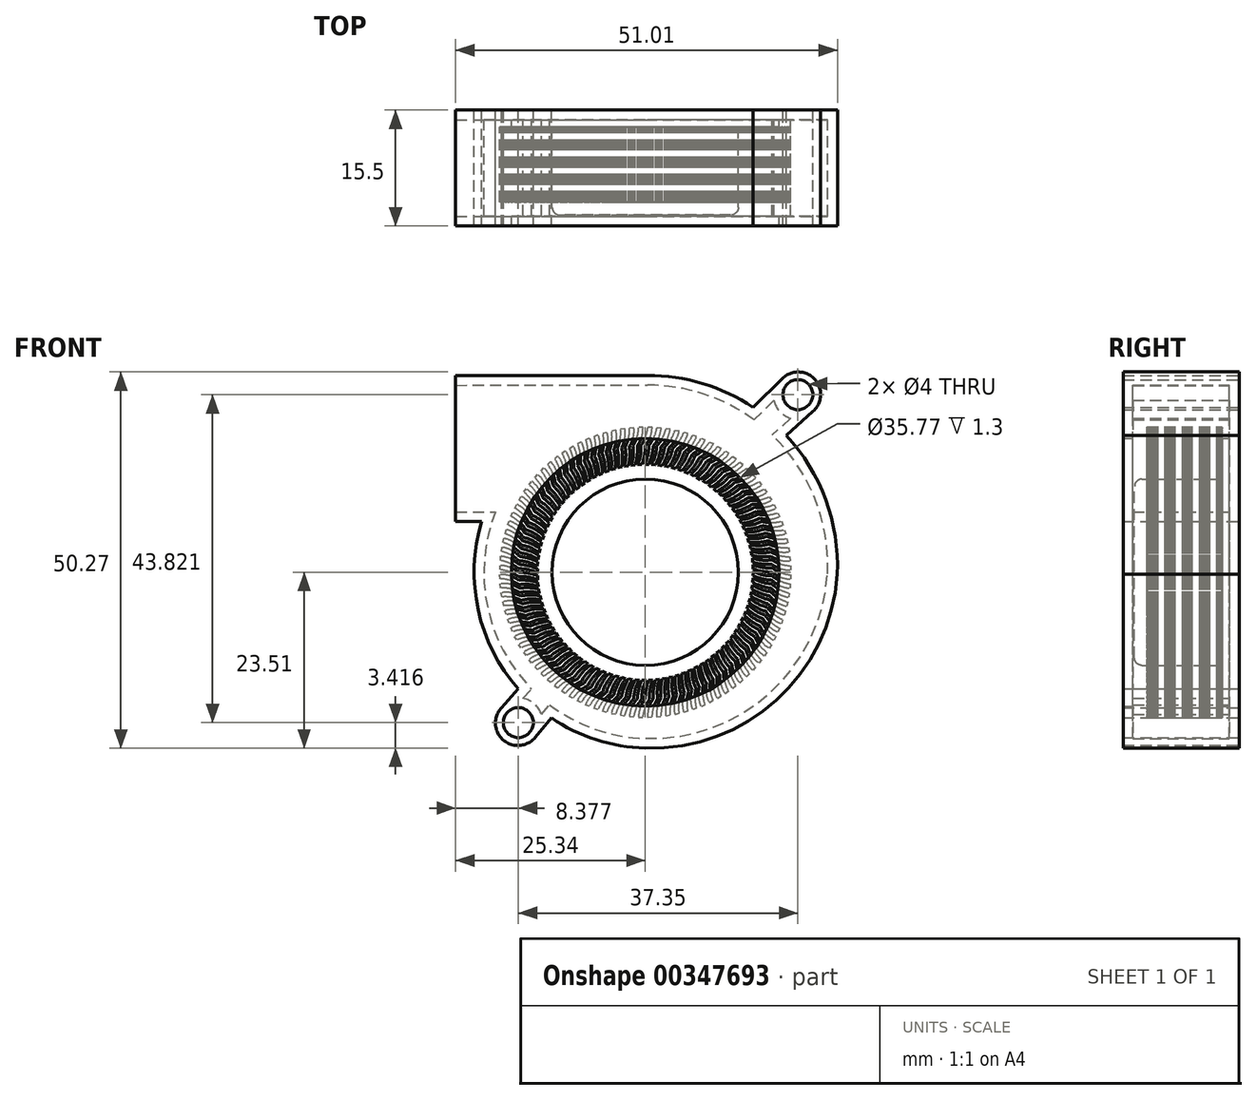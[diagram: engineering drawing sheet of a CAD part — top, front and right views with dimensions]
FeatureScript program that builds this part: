
annotation { "Feature Type Name" : "Feature", "Feature Type Description" : "" }
export const myFeature = defineFeature(function(context is Context, id is Id, definition is map)
    precondition{}
    {
        {
            var Q0;
            Q0=qCreatedBy(makeId("Front.planeOp"),FACE);
            var sketch = newSketch(context, id + "F0", { "sketchPlane" : qUnion([Q0])});
            skCircle(sketch, "E0", {"center": v(0, 0) * mm, "radius": 12.44 * mm});
            skCircle(sketch, "E1", {"center": v(0, 0) * mm, "radius": 15.98 * mm});
            skCircle(sketch, "E2.0", {"center": v(0, 0) * mm, "radius": 17.88 * mm});
            skLineSegment(sketch, "E3", {"start": v(-25.34, 6.78) * mm, "end": v(-25.34, 26.28) * mm});
            skLineSegment(sketch, "E4", {"start": v(-25.34, 6.78) * mm, "end": v(-21.86, 6.78) * mm});
            skLineSegment(sketch, "E5", {"start": v(-25.34, 26.28) * mm, "end": v(0.29, 26.3) * mm});
            skArc(sketch, "E6", {"start": v(25.64, -0.28) * mm, "mid": v(18.67, 18.45) * mm, "end": v(0.29, 26.3) * mm});
            skArc(sketch, "E7", {"start": v(0, -23.5) * mm, "mid": v(17.52, -17.08) * mm, "end": v(25.64, -0.28) * mm});
            skArc(sketch, "E8", {"start": v(-21.86, 6.78) * mm, "mid": v(-18.42, -13.77) * mm, "end": v(0, -23.5) * mm});
            skCircle(sketch, "E9", {"center": v(20.39, 23.73) * mm, "radius": 2 * mm});
            skCircle(sketch, "E10", {"center": v(-16.96, -20.1) * mm, "radius": 2 * mm});
            skLineSegment(sketch, "E11", {"start": v(22.42, 21.52) * mm, "end": v(18.83, 18.28) * mm});
            skLineSegment(sketch, "E12", {"start": v(18.32, 25.9) * mm, "end": v(14.4, 22.03) * mm});
            skArc(sketch, "E13", {"start": v(22.42, 21.52) * mm, "mid": v(22.61, 25.82) * mm, "end": v(18.32, 25.9) * mm});
            skLineSegment(sketch, "E14", {"start": v(-19.2, -18.1) * mm, "end": v(-16.96, -15.6) * mm});
            skLineSegment(sketch, "E15", {"start": v(-14.7, -22.06) * mm, "end": v(-12.56, -19.47) * mm});
            skArc(sketch, "E16", {"start": v(-19.2, -18.1) * mm, "mid": v(-19, -22.4) * mm, "end": v(-14.7, -22.06) * mm});
            skSolve(sketch);
        }
        {
            var Q0;
            Q0=makeQuery(id+"F0.imprint","IMPRINT",FACE,{"disambiguationData":[TD([[makeQuery(id+"F0.imprint","IMPRINT",EDGE,{"derivedFrom":sQuery(id+"F0.wireOp",EDGE,"E2.0")}),-1.0]])]});
            var Q1;
            Q1=makeQuery(id+"F0.imprint","IMPRINT",FACE,{"disambiguationData":[TD([[makeQuery(id+"F0.imprint","IMPRINT",EDGE,{"derivedFrom":sQuery(id+"F0.wireOp",EDGE,"E9")}),-1.0]])]});
            var Q2;
            Q2=makeQuery(id+"F0.imprint","IMPRINT",FACE,{"disambiguationData":[TD([[makeQuery(id+"F0.imprint","IMPRINT",EDGE,{"derivedFrom":sQuery(id+"F0.wireOp",EDGE,"E10")}),-1.0]])]});
            extrude(context, id + "F1", {"entities" : qUnion([Q0, Q1, Q2]), "depth" : 15.5 * mm});
        }
        {
            var Q0;
            Q0=makeQuery(id+"F1.opExtrude","SWEPT_FACE",FACE,{"disambiguationData":[OSD([sQuery(id+"F0.wireOp",EDGE,"E3")])]});
            var Q1;
            Q1=makeQuery(id+"F1.opExtrude","SWEPT_FACE",FACE,{"disambiguationData":[OSD([sQuery(id+"F0.wireOp",EDGE,"E2.0")])]});
            shell(context, id + "F2", {"entities" : qUnion([Q0, Q1]), "thickness" : 1.3 * mm});
        }
        {
            var Q0;
            Q0=makeQuery(id+"F0.imprint","IMPRINT",FACE,{"disambiguationData":[TD([[makeQuery(id+"F0.imprint","IMPRINT",EDGE,{"derivedFrom":sQuery(id+"F0.wireOp",EDGE,"E0")}),-1.0]])]});
            var Q1;
            Q1=makeQuery(id+"F0.imprint","IMPRINT",FACE,{"disambiguationData":[TD([[makeQuery(id+"F0.imprint","IMPRINT",EDGE,{"derivedFrom":sQuery(id+"F0.wireOp",EDGE,"E0")}),1.0]])]});
            extrude(context, id + "F3", {"entities" : qUnion([Q0, Q1]), "operationType" : NewBodyOperationType.ADD, "depth" : 1.3 * mm});
        }
        {
            var Q0;
            Q0=makeQuery(id+"F0.imprint","IMPRINT",FACE,{"disambiguationData":[TD([[makeQuery(id+"F0.imprint","IMPRINT",EDGE,{"derivedFrom":sQuery(id+"F0.wireOp",EDGE,"E1")}),-1.0]])]});
            var Q1;
            Q1=makeQuery(id+"F0.imprint","IMPRINT",FACE,{"disambiguationData":[TD([[makeQuery(id+"F0.imprint","IMPRINT",EDGE,{"derivedFrom":sQuery(id+"F0.wireOp",EDGE,"E0")}),-1.0]])]});
            var Q2;
            Q2=makeQuery(id+"F0.imprint","IMPRINT",FACE,{"disambiguationData":[TD([[makeQuery(id+"F0.imprint","IMPRINT",EDGE,{"derivedFrom":sQuery(id+"F0.wireOp",EDGE,"E0")}),1.0]])]});
            extrude(context, id + "F4", {"entities" : qUnion([Q0, Q1, Q2]), "depth" : 2.3 * mm});
        }
        {
            var Q0;
            Q0=makeQuery(id+"F0.imprint","IMPRINT",FACE,{"disambiguationData":[TD([[makeQuery(id+"F0.imprint","IMPRINT",EDGE,{"derivedFrom":sQuery(id+"F0.wireOp",EDGE,"E0")}),1.0]])]});
            extrude(context, id + "F5", {"entities" : qUnion([Q0]), "operationType" : NewBodyOperationType.ADD, "depth" : 14 * mm});
        }
        {
            var Q0;
            Q0=makeQuery(id+"F5.opExtrude","CAP_FACE",FACE,{"disambiguationData":[OSD([sQuery(id+"F0.wireOp",EDGE,"E0")])],"isStart":false});
            fillet(context, id + "F6", {"entities" : qUnion([Q0]), "radius" : 1 * mm, "tangentPropagation" : true, "allowEdgeOverflow" : false});
        }
        {
            var Q0;
            Q0=makeQuery(id+"F0.imprint","IMPRINT",FACE,{"disambiguationData":[TD([[makeQuery(id+"F0.imprint","IMPRINT",EDGE,{"derivedFrom":sQuery(id+"F0.wireOp",EDGE,"E1")}),-1.0]])]});
            extrude(context, id + "F7", {"entities" : qUnion([Q0]), "operationType" : NewBodyOperationType.ADD, "depth" : 1.3 * mm});
        }
        {
            var Q0;
            Q0=makeQuery(id+"F4.opExtrude","CAP_FACE",FACE,{"disambiguationData":[OSD([sQuery(id+"F0.wireOp",EDGE,"E2.0")])],"isStart":false});
            var sketch = newSketch(context, id + "F8", { "sketchPlane" : qUnion([Q0])});
            skLineSegment(sketch, "E17", {"start": v(-0.45, 14.4) * mm, "end": v(-1.01, 14.4) * mm});
            skLineSegment(sketch, "E18.MirrorCS", {"start": v(0.34, 19.42) * mm, "end": v(0.91, 19.42) * mm});
            skArc(sketch, "E19", {"start": v(-1.01, 14.4) * mm, "mid": v(-0.64, 15.64) * mm, "end": v(-0.6, 16.93) * mm});
            skArc(sketch, "E20", {"start": v(-0.6, 16.93) * mm, "mid": v(0.04, 18.11) * mm, "end": v(0.34, 19.42) * mm});
            skArc(sketch, "E21", {"start": v(0, 16.93) * mm, "mid": v(0.67, 18.1) * mm, "end": v(0.91, 19.42) * mm});
            skArc(sketch, "E22", {"start": v(-0.45, 14.4) * mm, "mid": v(-0.11, 15.65) * mm, "end": v(0, 16.93) * mm});
            skArc(sketch, "E23.1.0", {"start": v(-1.91, 14.31) * mm, "mid": v(-1.62, 15.57) * mm, "end": v(-1.66, 16.86) * mm});
            skArc(sketch, "E23.1.1", {"start": v(-1.66, 16.86) * mm, "mid": v(-1.1, 18.08) * mm, "end": v(-0.87, 19.4) * mm});
            skArc(sketch, "E23.1.2", {"start": v(-1.35, 14.35) * mm, "mid": v(-1.1, 15.61) * mm, "end": v(-1.06, 16.9) * mm});
            skArc(sketch, "E23.1.3", {"start": v(-1.06, 16.9) * mm, "mid": v(-0.47, 18.1) * mm, "end": v(-0.31, 19.44) * mm});
            skLineSegment(sketch, "E23.1.4", {"start": v(-1.35, 14.35) * mm, "end": v(-1.91, 14.31) * mm});
            skLineSegment(sketch, "E23.1.5", {"start": v(-0.87, 19.4) * mm, "end": v(-0.31, 19.44) * mm});
            skArc(sketch, "E23.2.0", {"start": v(-2.8, 14.16) * mm, "mid": v(-2.6, 15.44) * mm, "end": v(-2.71, 16.73) * mm});
            skArc(sketch, "E23.2.1", {"start": v(-2.71, 16.73) * mm, "mid": v(-2.23, 17.97) * mm, "end": v(-2.1, 19.3) * mm});
            skArc(sketch, "E23.2.2", {"start": v(-2.25, 14.23) * mm, "mid": v(-2.07, 15.51) * mm, "end": v(-2.12, 16.8) * mm});
            skArc(sketch, "E23.2.3", {"start": v(-2.12, 16.8) * mm, "mid": v(-1.6, 18.04) * mm, "end": v(-1.53, 19.38) * mm});
            skLineSegment(sketch, "E23.2.4", {"start": v(-2.25, 14.23) * mm, "end": v(-2.8, 14.16) * mm});
            skLineSegment(sketch, "E23.2.5", {"start": v(-2.1, 19.3) * mm, "end": v(-1.53, 19.38) * mm});
            skArc(sketch, "E23.3.0", {"start": v(-3.7, 13.96) * mm, "mid": v(-3.56, 15.24) * mm, "end": v(-3.76, 16.52) * mm});
            skArc(sketch, "E23.3.1", {"start": v(-3.76, 16.52) * mm, "mid": v(-3.35, 17.8) * mm, "end": v(-3.3, 19.14) * mm});
            skArc(sketch, "E23.3.2", {"start": v(-3.14, 14.06) * mm, "mid": v(-3.04, 15.35) * mm, "end": v(-3.17, 16.64) * mm});
            skArc(sketch, "E23.3.3", {"start": v(-3.17, 16.64) * mm, "mid": v(-2.74, 17.9) * mm, "end": v(-2.74, 19.24) * mm});
            skLineSegment(sketch, "E23.3.4", {"start": v(-3.14, 14.06) * mm, "end": v(-3.7, 13.96) * mm});
            skLineSegment(sketch, "E23.3.5", {"start": v(-3.3, 19.14) * mm, "end": v(-2.74, 19.24) * mm});
            skArc(sketch, "E23.4.0", {"start": v(-4.56, 13.7) * mm, "mid": v(-4.5, 15) * mm, "end": v(-4.79, 16.26) * mm});
            skArc(sketch, "E23.4.1", {"start": v(-4.79, 16.26) * mm, "mid": v(-4.46, 17.55) * mm, "end": v(-4.5, 18.9) * mm});
            skArc(sketch, "E23.4.2", {"start": v(-4.01, 13.84) * mm, "mid": v(-4, 15.13) * mm, "end": v(-4.21, 16.4) * mm});
            skArc(sketch, "E23.4.3", {"start": v(-4.21, 16.4) * mm, "mid": v(-3.85, 17.7) * mm, "end": v(-3.95, 19.03) * mm});
            skLineSegment(sketch, "E23.4.4", {"start": v(-4.01, 13.84) * mm, "end": v(-4.56, 13.7) * mm});
            skLineSegment(sketch, "E23.4.5", {"start": v(-4.5, 18.9) * mm, "end": v(-3.95, 19.03) * mm});
            skArc(sketch, "E23.5.0", {"start": v(-5.41, 13.38) * mm, "mid": v(-5.44, 14.68) * mm, "end": v(-5.8, 15.92) * mm});
            skArc(sketch, "E23.5.1", {"start": v(-5.8, 15.92) * mm, "mid": v(-5.56, 17.24) * mm, "end": v(-5.67, 18.57) * mm});
            skArc(sketch, "E23.5.2", {"start": v(-4.87, 13.56) * mm, "mid": v(-4.94, 14.85) * mm, "end": v(-5.23, 16.1) * mm});
            skArc(sketch, "E23.5.3", {"start": v(-5.23, 16.1) * mm, "mid": v(-4.96, 17.42) * mm, "end": v(-5.13, 18.75) * mm});
            skLineSegment(sketch, "E23.5.4", {"start": v(-4.87, 13.56) * mm, "end": v(-5.41, 13.38) * mm});
            skLineSegment(sketch, "E23.5.5", {"start": v(-5.67, 18.57) * mm, "end": v(-5.13, 18.75) * mm});
            skArc(sketch, "E23.6.0", {"start": v(-6.24, 13.02) * mm, "mid": v(-6.35, 14.3) * mm, "end": v(-6.79, 15.53) * mm});
            skArc(sketch, "E23.6.1", {"start": v(-6.79, 15.53) * mm, "mid": v(-6.63, 16.86) * mm, "end": v(-6.83, 18.18) * mm});
            skArc(sketch, "E23.6.2", {"start": v(-5.72, 13.23) * mm, "mid": v(-5.87, 14.5) * mm, "end": v(-6.23, 15.75) * mm});
            skArc(sketch, "E23.6.3", {"start": v(-6.23, 15.75) * mm, "mid": v(-6.04, 17.07) * mm, "end": v(-6.3, 18.39) * mm});
            skLineSegment(sketch, "E23.6.4", {"start": v(-5.72, 13.23) * mm, "end": v(-6.24, 13.02) * mm});
            skLineSegment(sketch, "E23.6.5", {"start": v(-6.83, 18.18) * mm, "end": v(-6.3, 18.39) * mm});
            skArc(sketch, "E23.7.0", {"start": v(-7.05, 12.6) * mm, "mid": v(-7.24, 13.88) * mm, "end": v(-7.75, 15.07) * mm});
            skArc(sketch, "E23.7.1", {"start": v(-7.75, 15.07) * mm, "mid": v(-7.67, 16.4) * mm, "end": v(-7.95, 17.72) * mm});
            skArc(sketch, "E23.7.2", {"start": v(-6.54, 12.84) * mm, "mid": v(-6.76, 14.11) * mm, "end": v(-7.21, 15.32) * mm});
            skArc(sketch, "E23.7.3", {"start": v(-7.21, 15.32) * mm, "mid": v(-7.1, 16.66) * mm, "end": v(-7.44, 17.96) * mm});
            skLineSegment(sketch, "E23.7.4", {"start": v(-6.54, 12.84) * mm, "end": v(-7.05, 12.6) * mm});
            skLineSegment(sketch, "E23.7.5", {"start": v(-7.95, 17.72) * mm, "end": v(-7.44, 17.96) * mm});
            skArc(sketch, "E23.8.0", {"start": v(-7.83, 12.13) * mm, "mid": v(-8.1, 13.4) * mm, "end": v(-8.68, 14.55) * mm});
            skArc(sketch, "E23.8.1", {"start": v(-8.68, 14.55) * mm, "mid": v(-8.69, 15.9) * mm, "end": v(-9.05, 17.18) * mm});
            skArc(sketch, "E23.8.2", {"start": v(-7.33, 12.4) * mm, "mid": v(-7.64, 13.66) * mm, "end": v(-8.16, 14.84) * mm});
            skArc(sketch, "E23.8.3", {"start": v(-8.16, 14.84) * mm, "mid": v(-8.13, 16.18) * mm, "end": v(-8.56, 17.45) * mm});
            skLineSegment(sketch, "E23.8.4", {"start": v(-7.33, 12.4) * mm, "end": v(-7.83, 12.13) * mm});
            skLineSegment(sketch, "E23.8.5", {"start": v(-9.05, 17.18) * mm, "end": v(-8.56, 17.45) * mm});
            skArc(sketch, "E23.9.0", {"start": v(-8.57, 11.62) * mm, "mid": v(-8.92, 12.86) * mm, "end": v(-9.58, 13.98) * mm});
            skArc(sketch, "E23.9.1", {"start": v(-9.58, 13.98) * mm, "mid": v(-9.67, 15.32) * mm, "end": v(-10.11, 16.58) * mm});
            skArc(sketch, "E23.9.2", {"start": v(-8.1, 11.92) * mm, "mid": v(-8.48, 13.15) * mm, "end": v(-9.07, 14.3) * mm});
            skArc(sketch, "E23.9.3", {"start": v(-9.07, 14.3) * mm, "mid": v(-9.13, 15.64) * mm, "end": v(-9.63, 16.88) * mm});
            skLineSegment(sketch, "E23.9.4", {"start": v(-8.1, 11.92) * mm, "end": v(-8.57, 11.62) * mm});
            skLineSegment(sketch, "E23.9.5", {"start": v(-10.11, 16.58) * mm, "end": v(-9.63, 16.88) * mm});
            skArc(sketch, "E23.10.0", {"start": v(-9.28, 11.06) * mm, "mid": v(-9.7, 12.28) * mm, "end": v(-10.43, 13.35) * mm});
            skArc(sketch, "E23.10.1", {"start": v(-10.43, 13.35) * mm, "mid": v(-10.61, 14.68) * mm, "end": v(-11.13, 15.91) * mm});
            skArc(sketch, "E23.10.2", {"start": v(-8.83, 11.39) * mm, "mid": v(-9.29, 12.6) * mm, "end": v(-9.95, 13.7) * mm});
            skArc(sketch, "E23.10.3", {"start": v(-9.95, 13.7) * mm, "mid": v(-10.1, 15.03) * mm, "end": v(-10.68, 16.24) * mm});
            skLineSegment(sketch, "E23.10.4", {"start": v(-8.83, 11.39) * mm, "end": v(-9.28, 11.06) * mm});
            skLineSegment(sketch, "E23.10.5", {"start": v(-11.13, 15.91) * mm, "end": v(-10.68, 16.24) * mm});
            skArc(sketch, "E23.11.0", {"start": v(-9.96, 10.45) * mm, "mid": v(-10.46, 11.65) * mm, "end": v(-11.25, 12.67) * mm});
            skArc(sketch, "E23.11.1", {"start": v(-11.25, 12.67) * mm, "mid": v(-11.51, 13.98) * mm, "end": v(-12.11, 15.18) * mm});
            skArc(sketch, "E23.11.2", {"start": v(-9.52, 10.81) * mm, "mid": v(-10.06, 11.99) * mm, "end": v(-10.8, 13.05) * mm});
            skArc(sketch, "E23.11.3", {"start": v(-10.8, 13.05) * mm, "mid": v(-11.02, 14.37) * mm, "end": v(-11.67, 15.54) * mm});
            skLineSegment(sketch, "E23.11.4", {"start": v(-9.52, 10.81) * mm, "end": v(-9.96, 10.45) * mm});
            skLineSegment(sketch, "E23.11.5", {"start": v(-12.11, 15.18) * mm, "end": v(-11.67, 15.54) * mm});
            skArc(sketch, "E23.12.0", {"start": v(-10.6, 9.8) * mm, "mid": v(-11.17, 10.97) * mm, "end": v(-12.03, 11.94) * mm});
            skArc(sketch, "E23.12.1", {"start": v(-12.03, 11.94) * mm, "mid": v(-12.37, 13.23) * mm, "end": v(-13.04, 14.39) * mm});
            skArc(sketch, "E23.12.2", {"start": v(-10.18, 10.2) * mm, "mid": v(-10.8, 11.33) * mm, "end": v(-11.6, 12.35) * mm});
            skArc(sketch, "E23.12.3", {"start": v(-11.6, 12.35) * mm, "mid": v(-11.9, 13.65) * mm, "end": v(-12.63, 14.78) * mm});
            skLineSegment(sketch, "E23.12.4", {"start": v(-10.18, 10.2) * mm, "end": v(-10.6, 9.8) * mm});
            skLineSegment(sketch, "E23.12.5", {"start": v(-13.04, 14.39) * mm, "end": v(-12.63, 14.78) * mm});
            skArc(sketch, "E23.13.0", {"start": v(-11.2, 9.12) * mm, "mid": v(-11.84, 10.24) * mm, "end": v(-12.75, 11.16) * mm});
            skArc(sketch, "E23.13.1", {"start": v(-12.75, 11.16) * mm, "mid": v(-13.17, 12.43) * mm, "end": v(-13.92, 13.54) * mm});
            skArc(sketch, "E23.13.2", {"start": v(-10.8, 9.53) * mm, "mid": v(-11.48, 10.63) * mm, "end": v(-12.35, 11.6) * mm});
            skArc(sketch, "E23.13.3", {"start": v(-12.35, 11.6) * mm, "mid": v(-12.74, 12.88) * mm, "end": v(-13.53, 13.96) * mm});
            skLineSegment(sketch, "E23.13.4", {"start": v(-10.8, 9.53) * mm, "end": v(-11.2, 9.12) * mm});
            skLineSegment(sketch, "E23.13.5", {"start": v(-13.92, 13.54) * mm, "end": v(-13.53, 13.96) * mm});
            skArc(sketch, "E23.14.0", {"start": v(-11.74, 8.4) * mm, "mid": v(-12.46, 9.48) * mm, "end": v(-13.43, 10.34) * mm});
            skArc(sketch, "E23.14.1", {"start": v(-13.43, 10.34) * mm, "mid": v(-13.93, 11.58) * mm, "end": v(-14.74, 12.64) * mm});
            skArc(sketch, "E23.14.2", {"start": v(-11.38, 8.84) * mm, "mid": v(-12.13, 9.89) * mm, "end": v(-13.05, 10.8) * mm});
            skArc(sketch, "E23.14.3", {"start": v(-13.05, 10.8) * mm, "mid": v(-13.52, 12.05) * mm, "end": v(-14.38, 13.08) * mm});
            skLineSegment(sketch, "E23.14.4", {"start": v(-11.38, 8.84) * mm, "end": v(-11.74, 8.4) * mm});
            skLineSegment(sketch, "E23.14.5", {"start": v(-14.74, 12.64) * mm, "end": v(-14.38, 13.08) * mm});
            skArc(sketch, "E23.15.0", {"start": v(-12.25, 7.65) * mm, "mid": v(-13.03, 8.68) * mm, "end": v(-14.05, 9.47) * mm});
            skArc(sketch, "E23.15.1", {"start": v(-14.05, 9.47) * mm, "mid": v(-14.63, 10.68) * mm, "end": v(-15.5, 11.7) * mm});
            skArc(sketch, "E23.15.2", {"start": v(-11.91, 8.1) * mm, "mid": v(-12.73, 9.1) * mm, "end": v(-13.7, 9.95) * mm});
            skArc(sketch, "E23.15.3", {"start": v(-13.7, 9.95) * mm, "mid": v(-14.25, 11.18) * mm, "end": v(-15.17, 12.15) * mm});
            skLineSegment(sketch, "E23.15.4", {"start": v(-11.91, 8.1) * mm, "end": v(-12.25, 7.65) * mm});
            skLineSegment(sketch, "E23.15.5", {"start": v(-15.5, 11.7) * mm, "end": v(-15.17, 12.15) * mm});
            skArc(sketch, "E23.16.0", {"start": v(-12.7, 6.86) * mm, "mid": v(-13.55, 7.84) * mm, "end": v(-14.62, 8.57) * mm});
            skArc(sketch, "E23.16.1", {"start": v(-14.62, 8.57) * mm, "mid": v(-15.27, 9.74) * mm, "end": v(-16.2, 10.7) * mm});
            skArc(sketch, "E23.16.2", {"start": v(-12.4, 7.34) * mm, "mid": v(-13.27, 8.3) * mm, "end": v(-14.3, 9.07) * mm});
            skArc(sketch, "E23.16.3", {"start": v(-14.3, 9.07) * mm, "mid": v(-14.92, 10.26) * mm, "end": v(-15.9, 11.17) * mm});
            skLineSegment(sketch, "E23.16.4", {"start": v(-12.4, 7.34) * mm, "end": v(-12.7, 6.86) * mm});
            skLineSegment(sketch, "E23.16.5", {"start": v(-16.2, 10.7) * mm, "end": v(-15.9, 11.17) * mm});
            skArc(sketch, "E23.17.0", {"start": v(-13.1, 6.05) * mm, "mid": v(-14.01, 6.98) * mm, "end": v(-15.13, 7.64) * mm});
            skArc(sketch, "E23.17.1", {"start": v(-15.13, 7.64) * mm, "mid": v(-15.85, 8.76) * mm, "end": v(-16.85, 9.66) * mm});
            skArc(sketch, "E23.17.2", {"start": v(-12.84, 6.55) * mm, "mid": v(-13.77, 7.44) * mm, "end": v(-14.84, 8.16) * mm});
            skArc(sketch, "E23.17.3", {"start": v(-14.84, 8.16) * mm, "mid": v(-15.54, 9.3) * mm, "end": v(-16.58, 10.15) * mm});
            skLineSegment(sketch, "E23.17.4", {"start": v(-12.84, 6.55) * mm, "end": v(-13.1, 6.05) * mm});
            skLineSegment(sketch, "E23.17.5", {"start": v(-16.85, 9.66) * mm, "end": v(-16.58, 10.15) * mm});
            skArc(sketch, "E23.18.0", {"start": v(-13.46, 5.22) * mm, "mid": v(-14.42, 6.08) * mm, "end": v(-15.58, 6.67) * mm});
            skArc(sketch, "E23.18.1", {"start": v(-15.58, 6.67) * mm, "mid": v(-16.37, 7.75) * mm, "end": v(-17.42, 8.58) * mm});
            skArc(sketch, "E23.18.2", {"start": v(-13.22, 5.73) * mm, "mid": v(-14.2, 6.56) * mm, "end": v(-15.32, 7.21) * mm});
            skArc(sketch, "E23.18.3", {"start": v(-15.32, 7.21) * mm, "mid": v(-16.1, 8.3) * mm, "end": v(-17.18, 9.1) * mm});
            skLineSegment(sketch, "E23.18.4", {"start": v(-13.22, 5.73) * mm, "end": v(-13.46, 5.22) * mm});
            skLineSegment(sketch, "E23.18.5", {"start": v(-17.42, 8.58) * mm, "end": v(-17.18, 9.1) * mm});
            skArc(sketch, "E23.19.0", {"start": v(-13.76, 4.36) * mm, "mid": v(-14.78, 5.16) * mm, "end": v(-15.96, 5.68) * mm});
            skArc(sketch, "E23.19.1", {"start": v(-15.96, 5.68) * mm, "mid": v(-16.82, 6.7) * mm, "end": v(-17.93, 7.47) * mm});
            skArc(sketch, "E23.19.2", {"start": v(-13.55, 4.89) * mm, "mid": v(-14.6, 5.66) * mm, "end": v(-15.75, 6.23) * mm});
            skArc(sketch, "E23.19.3", {"start": v(-15.75, 6.23) * mm, "mid": v(-16.58, 7.28) * mm, "end": v(-17.72, 8) * mm});
            skLineSegment(sketch, "E23.19.4", {"start": v(-13.55, 4.89) * mm, "end": v(-13.76, 4.36) * mm});
            skLineSegment(sketch, "E23.19.5", {"start": v(-17.93, 7.47) * mm, "end": v(-17.72, 8) * mm});
            skArc(sketch, "E23.20.0", {"start": v(-14, 3.49) * mm, "mid": v(-15.07, 4.23) * mm, "end": v(-16.29, 4.67) * mm});
            skArc(sketch, "E23.20.1", {"start": v(-16.29, 4.67) * mm, "mid": v(-17.21, 5.64) * mm, "end": v(-18.36, 6.33) * mm});
            skArc(sketch, "E23.20.2", {"start": v(-13.84, 4.03) * mm, "mid": v(-14.92, 4.73) * mm, "end": v(-16.1, 5.23) * mm});
            skArc(sketch, "E23.20.3", {"start": v(-16.1, 5.23) * mm, "mid": v(-17, 6.23) * mm, "end": v(-18.18, 6.87) * mm});
            skLineSegment(sketch, "E23.20.4", {"start": v(-13.84, 4.03) * mm, "end": v(-14, 3.49) * mm});
            skLineSegment(sketch, "E23.20.5", {"start": v(-18.36, 6.33) * mm, "end": v(-18.18, 6.87) * mm});
            skArc(sketch, "E23.21.0", {"start": v(-14.2, 2.6) * mm, "mid": v(-15.3, 3.27) * mm, "end": v(-16.55, 3.64) * mm});
            skArc(sketch, "E23.21.1", {"start": v(-16.55, 3.64) * mm, "mid": v(-17.53, 4.55) * mm, "end": v(-18.72, 5.16) * mm});
            skArc(sketch, "E23.21.2", {"start": v(-14.06, 3.15) * mm, "mid": v(-15.19, 3.78) * mm, "end": v(-16.4, 4.21) * mm});
            skArc(sketch, "E23.21.3", {"start": v(-16.4, 4.21) * mm, "mid": v(-17.36, 5.15) * mm, "end": v(-18.58, 5.71) * mm});
            skLineSegment(sketch, "E23.21.4", {"start": v(-14.06, 3.15) * mm, "end": v(-14.2, 2.6) * mm});
            skLineSegment(sketch, "E23.21.5", {"start": v(-18.72, 5.16) * mm, "end": v(-18.58, 5.71) * mm});
            skArc(sketch, "E23.22.0", {"start": v(-14.34, 1.7) * mm, "mid": v(-15.48, 2.3) * mm, "end": v(-16.75, 2.59) * mm});
            skArc(sketch, "E23.22.1", {"start": v(-16.75, 2.59) * mm, "mid": v(-17.78, 3.44) * mm, "end": v(-19, 3.98) * mm});
            skArc(sketch, "E23.22.2", {"start": v(-14.23, 2.26) * mm, "mid": v(-15.4, 2.82) * mm, "end": v(-16.64, 3.17) * mm});
            skArc(sketch, "E23.22.3", {"start": v(-16.64, 3.17) * mm, "mid": v(-17.65, 4.05) * mm, "end": v(-18.9, 4.53) * mm});
            skLineSegment(sketch, "E23.22.4", {"start": v(-14.23, 2.26) * mm, "end": v(-14.34, 1.7) * mm});
            skLineSegment(sketch, "E23.22.5", {"start": v(-19, 3.98) * mm, "end": v(-18.9, 4.53) * mm});
            skArc(sketch, "E23.23.0", {"start": v(-14.42, 0.8) * mm, "mid": v(-15.6, 1.33) * mm, "end": v(-16.88, 1.53) * mm});
            skArc(sketch, "E23.23.1", {"start": v(-16.88, 1.53) * mm, "mid": v(-17.96, 2.31) * mm, "end": v(-19.22, 2.78) * mm});
            skArc(sketch, "E23.23.2", {"start": v(-14.34, 1.36) * mm, "mid": v(-15.54, 1.85) * mm, "end": v(-16.8, 2.12) * mm});
            skArc(sketch, "E23.23.3", {"start": v(-16.8, 2.12) * mm, "mid": v(-17.87, 2.93) * mm, "end": v(-19.15, 3.34) * mm});
            skLineSegment(sketch, "E23.23.4", {"start": v(-14.34, 1.36) * mm, "end": v(-14.42, 0.8) * mm});
            skLineSegment(sketch, "E23.23.5", {"start": v(-19.22, 2.78) * mm, "end": v(-19.15, 3.34) * mm});
            skArc(sketch, "E23.24.0", {"start": v(-14.44, -0.1) * mm, "mid": v(-15.65, 0.35) * mm, "end": v(-16.94, 0.47) * mm});
            skArc(sketch, "E23.24.1", {"start": v(-16.94, 0.47) * mm, "mid": v(-18.07, 1.18) * mm, "end": v(-19.36, 1.56) * mm});
            skArc(sketch, "E23.24.2", {"start": v(-14.4, 0.46) * mm, "mid": v(-15.63, 0.87) * mm, "end": v(-16.9, 1.06) * mm});
            skArc(sketch, "E23.24.3", {"start": v(-16.9, 1.06) * mm, "mid": v(-18.02, 1.8) * mm, "end": v(-19.32, 2.13) * mm});
            skLineSegment(sketch, "E23.24.4", {"start": v(-14.4, 0.46) * mm, "end": v(-14.44, -0.1) * mm});
            skLineSegment(sketch, "E23.24.5", {"start": v(-19.36, 1.56) * mm, "end": v(-19.32, 2.13) * mm});
            skArc(sketch, "E23.25.0", {"start": v(-14.4, -1.01) * mm, "mid": v(-15.64, -0.64) * mm, "end": v(-16.93, -0.6) * mm});
            skArc(sketch, "E23.25.1", {"start": v(-16.93, -0.6) * mm, "mid": v(-18.11, 0.04) * mm, "end": v(-19.42, 0.34) * mm});
            skArc(sketch, "E23.25.2", {"start": v(-14.4, -0.45) * mm, "mid": v(-15.65, -0.11) * mm, "end": v(-16.93, 0) * mm});
            skArc(sketch, "E23.25.3", {"start": v(-16.93, 0) * mm, "mid": v(-18.1, 0.67) * mm, "end": v(-19.42, 0.91) * mm});
            skLineSegment(sketch, "E23.25.4", {"start": v(-14.4, -0.45) * mm, "end": v(-14.4, -1.01) * mm});
            skLineSegment(sketch, "E23.25.5", {"start": v(-19.42, 0.34) * mm, "end": v(-19.42, 0.91) * mm});
            skArc(sketch, "E23.26.0", {"start": v(-14.31, -1.91) * mm, "mid": v(-15.57, -1.62) * mm, "end": v(-16.86, -1.66) * mm});
            skArc(sketch, "E23.26.1", {"start": v(-16.86, -1.66) * mm, "mid": v(-18.08, -1.1) * mm, "end": v(-19.4, -0.87) * mm});
            skArc(sketch, "E23.26.2", {"start": v(-14.35, -1.35) * mm, "mid": v(-15.61, -1.1) * mm, "end": v(-16.9, -1.06) * mm});
            skArc(sketch, "E23.26.3", {"start": v(-16.9, -1.06) * mm, "mid": v(-18.1, -0.47) * mm, "end": v(-19.44, -0.31) * mm});
            skLineSegment(sketch, "E23.26.4", {"start": v(-14.35, -1.35) * mm, "end": v(-14.31, -1.91) * mm});
            skLineSegment(sketch, "E23.26.5", {"start": v(-19.4, -0.87) * mm, "end": v(-19.44, -0.31) * mm});
            skArc(sketch, "E23.27.0", {"start": v(-14.16, -2.8) * mm, "mid": v(-15.44, -2.6) * mm, "end": v(-16.73, -2.71) * mm});
            skArc(sketch, "E23.27.1", {"start": v(-16.73, -2.71) * mm, "mid": v(-17.97, -2.23) * mm, "end": v(-19.3, -2.1) * mm});
            skArc(sketch, "E23.27.2", {"start": v(-14.23, -2.25) * mm, "mid": v(-15.51, -2.07) * mm, "end": v(-16.8, -2.12) * mm});
            skArc(sketch, "E23.27.3", {"start": v(-16.8, -2.12) * mm, "mid": v(-18.04, -1.6) * mm, "end": v(-19.38, -1.53) * mm});
            skLineSegment(sketch, "E23.27.4", {"start": v(-14.23, -2.25) * mm, "end": v(-14.16, -2.8) * mm});
            skLineSegment(sketch, "E23.27.5", {"start": v(-19.3, -2.1) * mm, "end": v(-19.38, -1.53) * mm});
            skArc(sketch, "E23.28.0", {"start": v(-13.96, -3.7) * mm, "mid": v(-15.24, -3.56) * mm, "end": v(-16.52, -3.76) * mm});
            skArc(sketch, "E23.28.1", {"start": v(-16.52, -3.76) * mm, "mid": v(-17.8, -3.35) * mm, "end": v(-19.14, -3.3) * mm});
            skArc(sketch, "E23.28.2", {"start": v(-14.06, -3.14) * mm, "mid": v(-15.35, -3.04) * mm, "end": v(-16.64, -3.17) * mm});
            skArc(sketch, "E23.28.3", {"start": v(-16.64, -3.17) * mm, "mid": v(-17.9, -2.74) * mm, "end": v(-19.24, -2.74) * mm});
            skLineSegment(sketch, "E23.28.4", {"start": v(-14.06, -3.14) * mm, "end": v(-13.96, -3.7) * mm});
            skLineSegment(sketch, "E23.28.5", {"start": v(-19.14, -3.3) * mm, "end": v(-19.24, -2.74) * mm});
            skArc(sketch, "E23.29.0", {"start": v(-13.7, -4.56) * mm, "mid": v(-15, -4.5) * mm, "end": v(-16.26, -4.79) * mm});
            skArc(sketch, "E23.29.1", {"start": v(-16.26, -4.79) * mm, "mid": v(-17.55, -4.46) * mm, "end": v(-18.9, -4.5) * mm});
            skArc(sketch, "E23.29.2", {"start": v(-13.84, -4.01) * mm, "mid": v(-15.13, -4) * mm, "end": v(-16.4, -4.21) * mm});
            skArc(sketch, "E23.29.3", {"start": v(-16.4, -4.21) * mm, "mid": v(-17.7, -3.85) * mm, "end": v(-19.03, -3.95) * mm});
            skLineSegment(sketch, "E23.29.4", {"start": v(-13.84, -4.01) * mm, "end": v(-13.7, -4.56) * mm});
            skLineSegment(sketch, "E23.29.5", {"start": v(-18.9, -4.5) * mm, "end": v(-19.03, -3.95) * mm});
            skArc(sketch, "E23.30.0", {"start": v(-13.38, -5.41) * mm, "mid": v(-14.68, -5.44) * mm, "end": v(-15.92, -5.8) * mm});
            skArc(sketch, "E23.30.1", {"start": v(-15.92, -5.8) * mm, "mid": v(-17.24, -5.56) * mm, "end": v(-18.57, -5.67) * mm});
            skArc(sketch, "E23.30.2", {"start": v(-13.56, -4.87) * mm, "mid": v(-14.85, -4.94) * mm, "end": v(-16.1, -5.23) * mm});
            skArc(sketch, "E23.30.3", {"start": v(-16.1, -5.23) * mm, "mid": v(-17.42, -4.96) * mm, "end": v(-18.75, -5.13) * mm});
            skLineSegment(sketch, "E23.30.4", {"start": v(-13.56, -4.87) * mm, "end": v(-13.38, -5.41) * mm});
            skLineSegment(sketch, "E23.30.5", {"start": v(-18.57, -5.67) * mm, "end": v(-18.75, -5.13) * mm});
            skArc(sketch, "E23.31.0", {"start": v(-13.02, -6.24) * mm, "mid": v(-14.3, -6.35) * mm, "end": v(-15.53, -6.79) * mm});
            skArc(sketch, "E23.31.1", {"start": v(-15.53, -6.79) * mm, "mid": v(-16.86, -6.63) * mm, "end": v(-18.18, -6.83) * mm});
            skArc(sketch, "E23.31.2", {"start": v(-13.23, -5.72) * mm, "mid": v(-14.5, -5.87) * mm, "end": v(-15.75, -6.23) * mm});
            skArc(sketch, "E23.31.3", {"start": v(-15.75, -6.23) * mm, "mid": v(-17.07, -6.04) * mm, "end": v(-18.39, -6.3) * mm});
            skLineSegment(sketch, "E23.31.4", {"start": v(-13.23, -5.72) * mm, "end": v(-13.02, -6.24) * mm});
            skLineSegment(sketch, "E23.31.5", {"start": v(-18.18, -6.83) * mm, "end": v(-18.39, -6.3) * mm});
            skArc(sketch, "E23.32.0", {"start": v(-12.6, -7.05) * mm, "mid": v(-13.88, -7.24) * mm, "end": v(-15.07, -7.75) * mm});
            skArc(sketch, "E23.32.1", {"start": v(-15.07, -7.75) * mm, "mid": v(-16.4, -7.67) * mm, "end": v(-17.72, -7.95) * mm});
            skArc(sketch, "E23.32.2", {"start": v(-12.84, -6.54) * mm, "mid": v(-14.11, -6.76) * mm, "end": v(-15.32, -7.21) * mm});
            skArc(sketch, "E23.32.3", {"start": v(-15.32, -7.21) * mm, "mid": v(-16.66, -7.1) * mm, "end": v(-17.96, -7.44) * mm});
            skLineSegment(sketch, "E23.32.4", {"start": v(-12.84, -6.54) * mm, "end": v(-12.6, -7.05) * mm});
            skLineSegment(sketch, "E23.32.5", {"start": v(-17.72, -7.95) * mm, "end": v(-17.96, -7.44) * mm});
            skArc(sketch, "E23.33.0", {"start": v(-12.13, -7.83) * mm, "mid": v(-13.4, -8.1) * mm, "end": v(-14.55, -8.68) * mm});
            skArc(sketch, "E23.33.1", {"start": v(-14.55, -8.68) * mm, "mid": v(-15.9, -8.69) * mm, "end": v(-17.18, -9.05) * mm});
            skArc(sketch, "E23.33.2", {"start": v(-12.4, -7.33) * mm, "mid": v(-13.66, -7.64) * mm, "end": v(-14.84, -8.16) * mm});
            skArc(sketch, "E23.33.3", {"start": v(-14.84, -8.16) * mm, "mid": v(-16.18, -8.13) * mm, "end": v(-17.45, -8.56) * mm});
            skLineSegment(sketch, "E23.33.4", {"start": v(-12.4, -7.33) * mm, "end": v(-12.13, -7.83) * mm});
            skLineSegment(sketch, "E23.33.5", {"start": v(-17.18, -9.05) * mm, "end": v(-17.45, -8.56) * mm});
            skArc(sketch, "E23.34.0", {"start": v(-11.62, -8.57) * mm, "mid": v(-12.86, -8.92) * mm, "end": v(-13.98, -9.58) * mm});
            skArc(sketch, "E23.34.1", {"start": v(-13.98, -9.58) * mm, "mid": v(-15.32, -9.67) * mm, "end": v(-16.58, -10.11) * mm});
            skArc(sketch, "E23.34.2", {"start": v(-11.92, -8.1) * mm, "mid": v(-13.15, -8.48) * mm, "end": v(-14.3, -9.07) * mm});
            skArc(sketch, "E23.34.3", {"start": v(-14.3, -9.07) * mm, "mid": v(-15.64, -9.13) * mm, "end": v(-16.88, -9.63) * mm});
            skLineSegment(sketch, "E23.34.4", {"start": v(-11.92, -8.1) * mm, "end": v(-11.62, -8.57) * mm});
            skLineSegment(sketch, "E23.34.5", {"start": v(-16.58, -10.11) * mm, "end": v(-16.88, -9.63) * mm});
            skArc(sketch, "E23.35.0", {"start": v(-11.06, -9.28) * mm, "mid": v(-12.28, -9.7) * mm, "end": v(-13.35, -10.43) * mm});
            skArc(sketch, "E23.35.1", {"start": v(-13.35, -10.43) * mm, "mid": v(-14.68, -10.61) * mm, "end": v(-15.91, -11.13) * mm});
            skArc(sketch, "E23.35.2", {"start": v(-11.39, -8.83) * mm, "mid": v(-12.6, -9.29) * mm, "end": v(-13.7, -9.95) * mm});
            skArc(sketch, "E23.35.3", {"start": v(-13.7, -9.95) * mm, "mid": v(-15.03, -10.1) * mm, "end": v(-16.24, -10.68) * mm});
            skLineSegment(sketch, "E23.35.4", {"start": v(-11.39, -8.83) * mm, "end": v(-11.06, -9.28) * mm});
            skLineSegment(sketch, "E23.35.5", {"start": v(-15.91, -11.13) * mm, "end": v(-16.24, -10.68) * mm});
            skArc(sketch, "E23.36.0", {"start": v(-10.45, -9.96) * mm, "mid": v(-11.65, -10.46) * mm, "end": v(-12.67, -11.25) * mm});
            skArc(sketch, "E23.36.1", {"start": v(-12.67, -11.25) * mm, "mid": v(-13.98, -11.51) * mm, "end": v(-15.18, -12.11) * mm});
            skArc(sketch, "E23.36.2", {"start": v(-10.81, -9.52) * mm, "mid": v(-11.99, -10.06) * mm, "end": v(-13.05, -10.8) * mm});
            skArc(sketch, "E23.36.3", {"start": v(-13.05, -10.8) * mm, "mid": v(-14.37, -11.02) * mm, "end": v(-15.54, -11.67) * mm});
            skLineSegment(sketch, "E23.36.4", {"start": v(-10.81, -9.52) * mm, "end": v(-10.45, -9.96) * mm});
            skLineSegment(sketch, "E23.36.5", {"start": v(-15.18, -12.11) * mm, "end": v(-15.54, -11.67) * mm});
            skArc(sketch, "E23.37.0", {"start": v(-9.8, -10.6) * mm, "mid": v(-10.97, -11.17) * mm, "end": v(-11.94, -12.03) * mm});
            skArc(sketch, "E23.37.1", {"start": v(-11.94, -12.03) * mm, "mid": v(-13.23, -12.37) * mm, "end": v(-14.39, -13.04) * mm});
            skArc(sketch, "E23.37.2", {"start": v(-10.2, -10.18) * mm, "mid": v(-11.33, -10.8) * mm, "end": v(-12.35, -11.6) * mm});
            skArc(sketch, "E23.37.3", {"start": v(-12.35, -11.6) * mm, "mid": v(-13.65, -11.9) * mm, "end": v(-14.78, -12.63) * mm});
            skLineSegment(sketch, "E23.37.4", {"start": v(-10.2, -10.18) * mm, "end": v(-9.8, -10.6) * mm});
            skLineSegment(sketch, "E23.37.5", {"start": v(-14.39, -13.04) * mm, "end": v(-14.78, -12.63) * mm});
            skArc(sketch, "E23.38.0", {"start": v(-9.12, -11.2) * mm, "mid": v(-10.24, -11.84) * mm, "end": v(-11.16, -12.75) * mm});
            skArc(sketch, "E23.38.1", {"start": v(-11.16, -12.75) * mm, "mid": v(-12.43, -13.17) * mm, "end": v(-13.54, -13.92) * mm});
            skArc(sketch, "E23.38.2", {"start": v(-9.53, -10.8) * mm, "mid": v(-10.63, -11.48) * mm, "end": v(-11.6, -12.35) * mm});
            skArc(sketch, "E23.38.3", {"start": v(-11.6, -12.35) * mm, "mid": v(-12.88, -12.74) * mm, "end": v(-13.96, -13.53) * mm});
            skLineSegment(sketch, "E23.38.4", {"start": v(-9.53, -10.8) * mm, "end": v(-9.12, -11.2) * mm});
            skLineSegment(sketch, "E23.38.5", {"start": v(-13.54, -13.92) * mm, "end": v(-13.96, -13.53) * mm});
            skArc(sketch, "E23.39.0", {"start": v(-8.4, -11.74) * mm, "mid": v(-9.48, -12.46) * mm, "end": v(-10.34, -13.43) * mm});
            skArc(sketch, "E23.39.1", {"start": v(-10.34, -13.43) * mm, "mid": v(-11.58, -13.93) * mm, "end": v(-12.64, -14.74) * mm});
            skArc(sketch, "E23.39.2", {"start": v(-8.84, -11.38) * mm, "mid": v(-9.89, -12.13) * mm, "end": v(-10.8, -13.05) * mm});
            skArc(sketch, "E23.39.3", {"start": v(-10.8, -13.05) * mm, "mid": v(-12.05, -13.52) * mm, "end": v(-13.08, -14.38) * mm});
            skLineSegment(sketch, "E23.39.4", {"start": v(-8.84, -11.38) * mm, "end": v(-8.4, -11.74) * mm});
            skLineSegment(sketch, "E23.39.5", {"start": v(-12.64, -14.74) * mm, "end": v(-13.08, -14.38) * mm});
            skArc(sketch, "E23.40.0", {"start": v(-7.65, -12.25) * mm, "mid": v(-8.68, -13.03) * mm, "end": v(-9.47, -14.05) * mm});
            skArc(sketch, "E23.40.1", {"start": v(-9.47, -14.05) * mm, "mid": v(-10.68, -14.63) * mm, "end": v(-11.7, -15.5) * mm});
            skArc(sketch, "E23.40.2", {"start": v(-8.1, -11.91) * mm, "mid": v(-9.1, -12.73) * mm, "end": v(-9.95, -13.7) * mm});
            skArc(sketch, "E23.40.3", {"start": v(-9.95, -13.7) * mm, "mid": v(-11.18, -14.25) * mm, "end": v(-12.15, -15.17) * mm});
            skLineSegment(sketch, "E23.40.4", {"start": v(-8.1, -11.91) * mm, "end": v(-7.65, -12.25) * mm});
            skLineSegment(sketch, "E23.40.5", {"start": v(-11.7, -15.5) * mm, "end": v(-12.15, -15.17) * mm});
            skArc(sketch, "E23.41.0", {"start": v(-6.86, -12.7) * mm, "mid": v(-7.84, -13.55) * mm, "end": v(-8.57, -14.62) * mm});
            skArc(sketch, "E23.41.1", {"start": v(-8.57, -14.62) * mm, "mid": v(-9.74, -15.27) * mm, "end": v(-10.7, -16.2) * mm});
            skArc(sketch, "E23.41.2", {"start": v(-7.34, -12.4) * mm, "mid": v(-8.3, -13.27) * mm, "end": v(-9.07, -14.3) * mm});
            skArc(sketch, "E23.41.3", {"start": v(-9.07, -14.3) * mm, "mid": v(-10.26, -14.92) * mm, "end": v(-11.17, -15.9) * mm});
            skLineSegment(sketch, "E23.41.4", {"start": v(-7.34, -12.4) * mm, "end": v(-6.86, -12.7) * mm});
            skLineSegment(sketch, "E23.41.5", {"start": v(-10.7, -16.2) * mm, "end": v(-11.17, -15.9) * mm});
            skArc(sketch, "E23.42.0", {"start": v(-6.05, -13.1) * mm, "mid": v(-6.98, -14.01) * mm, "end": v(-7.64, -15.13) * mm});
            skArc(sketch, "E23.42.1", {"start": v(-7.64, -15.13) * mm, "mid": v(-8.76, -15.85) * mm, "end": v(-9.66, -16.85) * mm});
            skArc(sketch, "E23.42.2", {"start": v(-6.55, -12.84) * mm, "mid": v(-7.44, -13.77) * mm, "end": v(-8.16, -14.84) * mm});
            skArc(sketch, "E23.42.3", {"start": v(-8.16, -14.84) * mm, "mid": v(-9.3, -15.54) * mm, "end": v(-10.15, -16.58) * mm});
            skLineSegment(sketch, "E23.42.4", {"start": v(-6.55, -12.84) * mm, "end": v(-6.05, -13.1) * mm});
            skLineSegment(sketch, "E23.42.5", {"start": v(-9.66, -16.85) * mm, "end": v(-10.15, -16.58) * mm});
            skArc(sketch, "E23.43.0", {"start": v(-5.22, -13.46) * mm, "mid": v(-6.08, -14.42) * mm, "end": v(-6.67, -15.58) * mm});
            skArc(sketch, "E23.43.1", {"start": v(-6.67, -15.58) * mm, "mid": v(-7.75, -16.37) * mm, "end": v(-8.58, -17.42) * mm});
            skArc(sketch, "E23.43.2", {"start": v(-5.73, -13.22) * mm, "mid": v(-6.56, -14.2) * mm, "end": v(-7.21, -15.32) * mm});
            skArc(sketch, "E23.43.3", {"start": v(-7.21, -15.32) * mm, "mid": v(-8.3, -16.1) * mm, "end": v(-9.1, -17.18) * mm});
            skLineSegment(sketch, "E23.43.4", {"start": v(-5.73, -13.22) * mm, "end": v(-5.22, -13.46) * mm});
            skLineSegment(sketch, "E23.43.5", {"start": v(-8.58, -17.42) * mm, "end": v(-9.1, -17.18) * mm});
            skArc(sketch, "E23.44.0", {"start": v(-4.36, -13.76) * mm, "mid": v(-5.16, -14.78) * mm, "end": v(-5.68, -15.96) * mm});
            skArc(sketch, "E23.44.1", {"start": v(-5.68, -15.96) * mm, "mid": v(-6.7, -16.82) * mm, "end": v(-7.47, -17.93) * mm});
            skArc(sketch, "E23.44.2", {"start": v(-4.89, -13.55) * mm, "mid": v(-5.66, -14.6) * mm, "end": v(-6.23, -15.75) * mm});
            skArc(sketch, "E23.44.3", {"start": v(-6.23, -15.75) * mm, "mid": v(-7.28, -16.58) * mm, "end": v(-8, -17.72) * mm});
            skLineSegment(sketch, "E23.44.4", {"start": v(-4.89, -13.55) * mm, "end": v(-4.36, -13.76) * mm});
            skLineSegment(sketch, "E23.44.5", {"start": v(-7.47, -17.93) * mm, "end": v(-8, -17.72) * mm});
            skArc(sketch, "E23.45.0", {"start": v(-3.49, -14) * mm, "mid": v(-4.23, -15.07) * mm, "end": v(-4.67, -16.29) * mm});
            skArc(sketch, "E23.45.1", {"start": v(-4.67, -16.29) * mm, "mid": v(-5.64, -17.21) * mm, "end": v(-6.33, -18.36) * mm});
            skArc(sketch, "E23.45.2", {"start": v(-4.03, -13.84) * mm, "mid": v(-4.73, -14.92) * mm, "end": v(-5.23, -16.1) * mm});
            skArc(sketch, "E23.45.3", {"start": v(-5.23, -16.1) * mm, "mid": v(-6.23, -17) * mm, "end": v(-6.87, -18.18) * mm});
            skLineSegment(sketch, "E23.45.4", {"start": v(-4.03, -13.84) * mm, "end": v(-3.49, -14) * mm});
            skLineSegment(sketch, "E23.45.5", {"start": v(-6.33, -18.36) * mm, "end": v(-6.87, -18.18) * mm});
            skArc(sketch, "E23.46.0", {"start": v(-2.6, -14.2) * mm, "mid": v(-3.27, -15.3) * mm, "end": v(-3.64, -16.55) * mm});
            skArc(sketch, "E23.46.1", {"start": v(-3.64, -16.55) * mm, "mid": v(-4.55, -17.53) * mm, "end": v(-5.16, -18.72) * mm});
            skArc(sketch, "E23.46.2", {"start": v(-3.15, -14.06) * mm, "mid": v(-3.78, -15.19) * mm, "end": v(-4.21, -16.4) * mm});
            skArc(sketch, "E23.46.3", {"start": v(-4.21, -16.4) * mm, "mid": v(-5.15, -17.36) * mm, "end": v(-5.71, -18.58) * mm});
            skLineSegment(sketch, "E23.46.4", {"start": v(-3.15, -14.06) * mm, "end": v(-2.6, -14.2) * mm});
            skLineSegment(sketch, "E23.46.5", {"start": v(-5.16, -18.72) * mm, "end": v(-5.71, -18.58) * mm});
            skArc(sketch, "E23.47.0", {"start": v(-1.7, -14.34) * mm, "mid": v(-2.3, -15.48) * mm, "end": v(-2.59, -16.75) * mm});
            skArc(sketch, "E23.47.1", {"start": v(-2.59, -16.75) * mm, "mid": v(-3.44, -17.78) * mm, "end": v(-3.98, -19) * mm});
            skArc(sketch, "E23.47.2", {"start": v(-2.26, -14.23) * mm, "mid": v(-2.82, -15.4) * mm, "end": v(-3.17, -16.64) * mm});
            skArc(sketch, "E23.47.3", {"start": v(-3.17, -16.64) * mm, "mid": v(-4.05, -17.65) * mm, "end": v(-4.53, -18.9) * mm});
            skLineSegment(sketch, "E23.47.4", {"start": v(-2.26, -14.23) * mm, "end": v(-1.7, -14.34) * mm});
            skLineSegment(sketch, "E23.47.5", {"start": v(-3.98, -19) * mm, "end": v(-4.53, -18.9) * mm});
            skArc(sketch, "E23.48.0", {"start": v(-0.8, -14.42) * mm, "mid": v(-1.33, -15.6) * mm, "end": v(-1.53, -16.88) * mm});
            skArc(sketch, "E23.48.1", {"start": v(-1.53, -16.88) * mm, "mid": v(-2.31, -17.96) * mm, "end": v(-2.78, -19.22) * mm});
            skArc(sketch, "E23.48.2", {"start": v(-1.36, -14.34) * mm, "mid": v(-1.85, -15.54) * mm, "end": v(-2.12, -16.8) * mm});
            skArc(sketch, "E23.48.3", {"start": v(-2.12, -16.8) * mm, "mid": v(-2.93, -17.87) * mm, "end": v(-3.34, -19.15) * mm});
            skLineSegment(sketch, "E23.48.4", {"start": v(-1.36, -14.34) * mm, "end": v(-0.8, -14.42) * mm});
            skLineSegment(sketch, "E23.48.5", {"start": v(-2.78, -19.22) * mm, "end": v(-3.34, -19.15) * mm});
            skArc(sketch, "E23.49.0", {"start": v(0.1, -14.44) * mm, "mid": v(-0.35, -15.65) * mm, "end": v(-0.47, -16.94) * mm});
            skArc(sketch, "E23.49.1", {"start": v(-0.47, -16.94) * mm, "mid": v(-1.18, -18.07) * mm, "end": v(-1.56, -19.36) * mm});
            skArc(sketch, "E23.49.2", {"start": v(-0.46, -14.4) * mm, "mid": v(-0.87, -15.63) * mm, "end": v(-1.06, -16.9) * mm});
            skArc(sketch, "E23.49.3", {"start": v(-1.06, -16.9) * mm, "mid": v(-1.8, -18.02) * mm, "end": v(-2.13, -19.32) * mm});
            skLineSegment(sketch, "E23.49.4", {"start": v(-0.46, -14.4) * mm, "end": v(0.1, -14.44) * mm});
            skLineSegment(sketch, "E23.49.5", {"start": v(-1.56, -19.36) * mm, "end": v(-2.13, -19.32) * mm});
            skArc(sketch, "E23.50.0", {"start": v(1.01, -14.4) * mm, "mid": v(0.64, -15.64) * mm, "end": v(0.6, -16.93) * mm});
            skArc(sketch, "E23.50.1", {"start": v(0.6, -16.93) * mm, "mid": v(-0.04, -18.11) * mm, "end": v(-0.34, -19.42) * mm});
            skArc(sketch, "E23.50.2", {"start": v(0.45, -14.4) * mm, "mid": v(0.11, -15.65) * mm, "end": v(0, -16.93) * mm});
            skArc(sketch, "E23.50.3", {"start": v(0, -16.93) * mm, "mid": v(-0.67, -18.1) * mm, "end": v(-0.91, -19.42) * mm});
            skLineSegment(sketch, "E23.50.4", {"start": v(0.45, -14.4) * mm, "end": v(1.01, -14.4) * mm});
            skLineSegment(sketch, "E23.50.5", {"start": v(-0.34, -19.42) * mm, "end": v(-0.91, -19.42) * mm});
            skArc(sketch, "E23.51.0", {"start": v(1.91, -14.31) * mm, "mid": v(1.62, -15.57) * mm, "end": v(1.66, -16.86) * mm});
            skArc(sketch, "E23.51.1", {"start": v(1.66, -16.86) * mm, "mid": v(1.1, -18.08) * mm, "end": v(0.87, -19.4) * mm});
            skArc(sketch, "E23.51.2", {"start": v(1.35, -14.35) * mm, "mid": v(1.1, -15.61) * mm, "end": v(1.06, -16.9) * mm});
            skArc(sketch, "E23.51.3", {"start": v(1.06, -16.9) * mm, "mid": v(0.47, -18.1) * mm, "end": v(0.31, -19.44) * mm});
            skLineSegment(sketch, "E23.51.4", {"start": v(1.35, -14.35) * mm, "end": v(1.91, -14.31) * mm});
            skLineSegment(sketch, "E23.51.5", {"start": v(0.87, -19.4) * mm, "end": v(0.31, -19.44) * mm});
            skArc(sketch, "E23.52.0", {"start": v(2.8, -14.16) * mm, "mid": v(2.6, -15.44) * mm, "end": v(2.71, -16.73) * mm});
            skArc(sketch, "E23.52.1", {"start": v(2.71, -16.73) * mm, "mid": v(2.23, -17.97) * mm, "end": v(2.1, -19.3) * mm});
            skArc(sketch, "E23.52.2", {"start": v(2.25, -14.23) * mm, "mid": v(2.07, -15.51) * mm, "end": v(2.12, -16.8) * mm});
            skArc(sketch, "E23.52.3", {"start": v(2.12, -16.8) * mm, "mid": v(1.6, -18.04) * mm, "end": v(1.53, -19.38) * mm});
            skLineSegment(sketch, "E23.52.4", {"start": v(2.25, -14.23) * mm, "end": v(2.8, -14.16) * mm});
            skLineSegment(sketch, "E23.52.5", {"start": v(2.1, -19.3) * mm, "end": v(1.53, -19.38) * mm});
            skArc(sketch, "E23.53.0", {"start": v(3.7, -13.96) * mm, "mid": v(3.56, -15.24) * mm, "end": v(3.76, -16.52) * mm});
            skArc(sketch, "E23.53.1", {"start": v(3.76, -16.52) * mm, "mid": v(3.35, -17.8) * mm, "end": v(3.3, -19.14) * mm});
            skArc(sketch, "E23.53.2", {"start": v(3.14, -14.06) * mm, "mid": v(3.04, -15.35) * mm, "end": v(3.17, -16.64) * mm});
            skArc(sketch, "E23.53.3", {"start": v(3.17, -16.64) * mm, "mid": v(2.74, -17.9) * mm, "end": v(2.74, -19.24) * mm});
            skLineSegment(sketch, "E23.53.4", {"start": v(3.14, -14.06) * mm, "end": v(3.7, -13.96) * mm});
            skLineSegment(sketch, "E23.53.5", {"start": v(3.3, -19.14) * mm, "end": v(2.74, -19.24) * mm});
            skArc(sketch, "E23.54.0", {"start": v(4.56, -13.7) * mm, "mid": v(4.5, -15) * mm, "end": v(4.79, -16.26) * mm});
            skArc(sketch, "E23.54.1", {"start": v(4.79, -16.26) * mm, "mid": v(4.46, -17.55) * mm, "end": v(4.5, -18.9) * mm});
            skArc(sketch, "E23.54.2", {"start": v(4.01, -13.84) * mm, "mid": v(4, -15.13) * mm, "end": v(4.21, -16.4) * mm});
            skArc(sketch, "E23.54.3", {"start": v(4.21, -16.4) * mm, "mid": v(3.85, -17.7) * mm, "end": v(3.95, -19.03) * mm});
            skLineSegment(sketch, "E23.54.4", {"start": v(4.01, -13.84) * mm, "end": v(4.56, -13.7) * mm});
            skLineSegment(sketch, "E23.54.5", {"start": v(4.5, -18.9) * mm, "end": v(3.95, -19.03) * mm});
            skArc(sketch, "E23.55.0", {"start": v(5.41, -13.38) * mm, "mid": v(5.44, -14.68) * mm, "end": v(5.8, -15.92) * mm});
            skArc(sketch, "E23.55.1", {"start": v(5.8, -15.92) * mm, "mid": v(5.56, -17.24) * mm, "end": v(5.67, -18.57) * mm});
            skArc(sketch, "E23.55.2", {"start": v(4.87, -13.56) * mm, "mid": v(4.94, -14.85) * mm, "end": v(5.23, -16.1) * mm});
            skArc(sketch, "E23.55.3", {"start": v(5.23, -16.1) * mm, "mid": v(4.96, -17.42) * mm, "end": v(5.13, -18.75) * mm});
            skLineSegment(sketch, "E23.55.4", {"start": v(4.87, -13.56) * mm, "end": v(5.41, -13.38) * mm});
            skLineSegment(sketch, "E23.55.5", {"start": v(5.67, -18.57) * mm, "end": v(5.13, -18.75) * mm});
            skArc(sketch, "E23.56.0", {"start": v(6.24, -13.02) * mm, "mid": v(6.35, -14.3) * mm, "end": v(6.79, -15.53) * mm});
            skArc(sketch, "E23.56.1", {"start": v(6.79, -15.53) * mm, "mid": v(6.63, -16.86) * mm, "end": v(6.83, -18.18) * mm});
            skArc(sketch, "E23.56.2", {"start": v(5.72, -13.23) * mm, "mid": v(5.87, -14.5) * mm, "end": v(6.23, -15.75) * mm});
            skArc(sketch, "E23.56.3", {"start": v(6.23, -15.75) * mm, "mid": v(6.04, -17.07) * mm, "end": v(6.3, -18.39) * mm});
            skLineSegment(sketch, "E23.56.4", {"start": v(5.72, -13.23) * mm, "end": v(6.24, -13.02) * mm});
            skLineSegment(sketch, "E23.56.5", {"start": v(6.83, -18.18) * mm, "end": v(6.3, -18.39) * mm});
            skArc(sketch, "E23.57.0", {"start": v(7.05, -12.6) * mm, "mid": v(7.24, -13.88) * mm, "end": v(7.75, -15.07) * mm});
            skArc(sketch, "E23.57.1", {"start": v(7.75, -15.07) * mm, "mid": v(7.67, -16.4) * mm, "end": v(7.95, -17.72) * mm});
            skArc(sketch, "E23.57.2", {"start": v(6.54, -12.84) * mm, "mid": v(6.76, -14.11) * mm, "end": v(7.21, -15.32) * mm});
            skArc(sketch, "E23.57.3", {"start": v(7.21, -15.32) * mm, "mid": v(7.1, -16.66) * mm, "end": v(7.44, -17.96) * mm});
            skLineSegment(sketch, "E23.57.4", {"start": v(6.54, -12.84) * mm, "end": v(7.05, -12.6) * mm});
            skLineSegment(sketch, "E23.57.5", {"start": v(7.95, -17.72) * mm, "end": v(7.44, -17.96) * mm});
            skArc(sketch, "E23.58.0", {"start": v(7.83, -12.13) * mm, "mid": v(8.1, -13.4) * mm, "end": v(8.68, -14.55) * mm});
            skArc(sketch, "E23.58.1", {"start": v(8.68, -14.55) * mm, "mid": v(8.69, -15.9) * mm, "end": v(9.05, -17.18) * mm});
            skArc(sketch, "E23.58.2", {"start": v(7.33, -12.4) * mm, "mid": v(7.64, -13.66) * mm, "end": v(8.16, -14.84) * mm});
            skArc(sketch, "E23.58.3", {"start": v(8.16, -14.84) * mm, "mid": v(8.13, -16.18) * mm, "end": v(8.56, -17.45) * mm});
            skLineSegment(sketch, "E23.58.4", {"start": v(7.33, -12.4) * mm, "end": v(7.83, -12.13) * mm});
            skLineSegment(sketch, "E23.58.5", {"start": v(9.05, -17.18) * mm, "end": v(8.56, -17.45) * mm});
            skArc(sketch, "E23.59.0", {"start": v(8.57, -11.62) * mm, "mid": v(8.92, -12.86) * mm, "end": v(9.58, -13.98) * mm});
            skArc(sketch, "E23.59.1", {"start": v(9.58, -13.98) * mm, "mid": v(9.67, -15.32) * mm, "end": v(10.11, -16.58) * mm});
            skArc(sketch, "E23.59.2", {"start": v(8.1, -11.92) * mm, "mid": v(8.48, -13.15) * mm, "end": v(9.07, -14.3) * mm});
            skArc(sketch, "E23.59.3", {"start": v(9.07, -14.3) * mm, "mid": v(9.13, -15.64) * mm, "end": v(9.63, -16.88) * mm});
            skLineSegment(sketch, "E23.59.4", {"start": v(8.1, -11.92) * mm, "end": v(8.57, -11.62) * mm});
            skLineSegment(sketch, "E23.59.5", {"start": v(10.11, -16.58) * mm, "end": v(9.63, -16.88) * mm});
            skArc(sketch, "E23.60.0", {"start": v(9.28, -11.06) * mm, "mid": v(9.7, -12.28) * mm, "end": v(10.43, -13.35) * mm});
            skArc(sketch, "E23.60.1", {"start": v(10.43, -13.35) * mm, "mid": v(10.61, -14.68) * mm, "end": v(11.13, -15.91) * mm});
            skArc(sketch, "E23.60.2", {"start": v(8.83, -11.39) * mm, "mid": v(9.29, -12.6) * mm, "end": v(9.95, -13.7) * mm});
            skArc(sketch, "E23.60.3", {"start": v(9.95, -13.7) * mm, "mid": v(10.1, -15.03) * mm, "end": v(10.68, -16.24) * mm});
            skLineSegment(sketch, "E23.60.4", {"start": v(8.83, -11.39) * mm, "end": v(9.28, -11.06) * mm});
            skLineSegment(sketch, "E23.60.5", {"start": v(11.13, -15.91) * mm, "end": v(10.68, -16.24) * mm});
            skArc(sketch, "E23.61.0", {"start": v(9.96, -10.45) * mm, "mid": v(10.46, -11.65) * mm, "end": v(11.25, -12.67) * mm});
            skArc(sketch, "E23.61.1", {"start": v(11.25, -12.67) * mm, "mid": v(11.51, -13.98) * mm, "end": v(12.11, -15.18) * mm});
            skArc(sketch, "E23.61.2", {"start": v(9.52, -10.81) * mm, "mid": v(10.06, -11.99) * mm, "end": v(10.8, -13.05) * mm});
            skArc(sketch, "E23.61.3", {"start": v(10.8, -13.05) * mm, "mid": v(11.02, -14.37) * mm, "end": v(11.67, -15.54) * mm});
            skLineSegment(sketch, "E23.61.4", {"start": v(9.52, -10.81) * mm, "end": v(9.96, -10.45) * mm});
            skLineSegment(sketch, "E23.61.5", {"start": v(12.11, -15.18) * mm, "end": v(11.67, -15.54) * mm});
            skArc(sketch, "E23.62.0", {"start": v(10.6, -9.8) * mm, "mid": v(11.17, -10.97) * mm, "end": v(12.03, -11.94) * mm});
            skArc(sketch, "E23.62.1", {"start": v(12.03, -11.94) * mm, "mid": v(12.37, -13.23) * mm, "end": v(13.04, -14.39) * mm});
            skArc(sketch, "E23.62.2", {"start": v(10.18, -10.2) * mm, "mid": v(10.8, -11.33) * mm, "end": v(11.6, -12.35) * mm});
            skArc(sketch, "E23.62.3", {"start": v(11.6, -12.35) * mm, "mid": v(11.9, -13.65) * mm, "end": v(12.63, -14.78) * mm});
            skLineSegment(sketch, "E23.62.4", {"start": v(10.18, -10.2) * mm, "end": v(10.6, -9.8) * mm});
            skLineSegment(sketch, "E23.62.5", {"start": v(13.04, -14.39) * mm, "end": v(12.63, -14.78) * mm});
            skArc(sketch, "E23.63.0", {"start": v(11.2, -9.12) * mm, "mid": v(11.84, -10.24) * mm, "end": v(12.75, -11.16) * mm});
            skArc(sketch, "E23.63.1", {"start": v(12.75, -11.16) * mm, "mid": v(13.17, -12.43) * mm, "end": v(13.92, -13.54) * mm});
            skArc(sketch, "E23.63.2", {"start": v(10.8, -9.53) * mm, "mid": v(11.48, -10.63) * mm, "end": v(12.35, -11.6) * mm});
            skArc(sketch, "E23.63.3", {"start": v(12.35, -11.6) * mm, "mid": v(12.74, -12.88) * mm, "end": v(13.53, -13.96) * mm});
            skLineSegment(sketch, "E23.63.4", {"start": v(10.8, -9.53) * mm, "end": v(11.2, -9.12) * mm});
            skLineSegment(sketch, "E23.63.5", {"start": v(13.92, -13.54) * mm, "end": v(13.53, -13.96) * mm});
            skArc(sketch, "E23.64.0", {"start": v(11.74, -8.4) * mm, "mid": v(12.46, -9.48) * mm, "end": v(13.43, -10.34) * mm});
            skArc(sketch, "E23.64.1", {"start": v(13.43, -10.34) * mm, "mid": v(13.93, -11.58) * mm, "end": v(14.74, -12.64) * mm});
            skArc(sketch, "E23.64.2", {"start": v(11.38, -8.84) * mm, "mid": v(12.13, -9.89) * mm, "end": v(13.05, -10.8) * mm});
            skArc(sketch, "E23.64.3", {"start": v(13.05, -10.8) * mm, "mid": v(13.52, -12.05) * mm, "end": v(14.38, -13.08) * mm});
            skLineSegment(sketch, "E23.64.4", {"start": v(11.38, -8.84) * mm, "end": v(11.74, -8.4) * mm});
            skLineSegment(sketch, "E23.64.5", {"start": v(14.74, -12.64) * mm, "end": v(14.38, -13.08) * mm});
            skArc(sketch, "E23.65.0", {"start": v(12.25, -7.65) * mm, "mid": v(13.03, -8.68) * mm, "end": v(14.05, -9.47) * mm});
            skArc(sketch, "E23.65.1", {"start": v(14.05, -9.47) * mm, "mid": v(14.63, -10.68) * mm, "end": v(15.5, -11.7) * mm});
            skArc(sketch, "E23.65.2", {"start": v(11.91, -8.1) * mm, "mid": v(12.73, -9.1) * mm, "end": v(13.7, -9.95) * mm});
            skArc(sketch, "E23.65.3", {"start": v(13.7, -9.95) * mm, "mid": v(14.25, -11.18) * mm, "end": v(15.17, -12.15) * mm});
            skLineSegment(sketch, "E23.65.4", {"start": v(11.91, -8.1) * mm, "end": v(12.25, -7.65) * mm});
            skLineSegment(sketch, "E23.65.5", {"start": v(15.5, -11.7) * mm, "end": v(15.17, -12.15) * mm});
            skArc(sketch, "E23.66.0", {"start": v(12.7, -6.86) * mm, "mid": v(13.55, -7.84) * mm, "end": v(14.62, -8.57) * mm});
            skArc(sketch, "E23.66.1", {"start": v(14.62, -8.57) * mm, "mid": v(15.27, -9.74) * mm, "end": v(16.2, -10.7) * mm});
            skArc(sketch, "E23.66.2", {"start": v(12.4, -7.34) * mm, "mid": v(13.27, -8.3) * mm, "end": v(14.3, -9.07) * mm});
            skArc(sketch, "E23.66.3", {"start": v(14.3, -9.07) * mm, "mid": v(14.92, -10.26) * mm, "end": v(15.9, -11.17) * mm});
            skLineSegment(sketch, "E23.66.4", {"start": v(12.4, -7.34) * mm, "end": v(12.7, -6.86) * mm});
            skLineSegment(sketch, "E23.66.5", {"start": v(16.2, -10.7) * mm, "end": v(15.9, -11.17) * mm});
            skArc(sketch, "E23.67.0", {"start": v(13.1, -6.05) * mm, "mid": v(14.01, -6.98) * mm, "end": v(15.13, -7.64) * mm});
            skArc(sketch, "E23.67.1", {"start": v(15.13, -7.64) * mm, "mid": v(15.85, -8.76) * mm, "end": v(16.85, -9.66) * mm});
            skArc(sketch, "E23.67.2", {"start": v(12.84, -6.55) * mm, "mid": v(13.77, -7.44) * mm, "end": v(14.84, -8.16) * mm});
            skArc(sketch, "E23.67.3", {"start": v(14.84, -8.16) * mm, "mid": v(15.54, -9.3) * mm, "end": v(16.58, -10.15) * mm});
            skLineSegment(sketch, "E23.67.4", {"start": v(12.84, -6.55) * mm, "end": v(13.1, -6.05) * mm});
            skLineSegment(sketch, "E23.67.5", {"start": v(16.85, -9.66) * mm, "end": v(16.58, -10.15) * mm});
            skArc(sketch, "E23.68.0", {"start": v(13.46, -5.22) * mm, "mid": v(14.42, -6.08) * mm, "end": v(15.58, -6.67) * mm});
            skArc(sketch, "E23.68.1", {"start": v(15.58, -6.67) * mm, "mid": v(16.37, -7.75) * mm, "end": v(17.42, -8.58) * mm});
            skArc(sketch, "E23.68.2", {"start": v(13.22, -5.73) * mm, "mid": v(14.2, -6.56) * mm, "end": v(15.32, -7.21) * mm});
            skArc(sketch, "E23.68.3", {"start": v(15.32, -7.21) * mm, "mid": v(16.1, -8.3) * mm, "end": v(17.18, -9.1) * mm});
            skLineSegment(sketch, "E23.68.4", {"start": v(13.22, -5.73) * mm, "end": v(13.46, -5.22) * mm});
            skLineSegment(sketch, "E23.68.5", {"start": v(17.42, -8.58) * mm, "end": v(17.18, -9.1) * mm});
            skArc(sketch, "E23.69.0", {"start": v(13.76, -4.36) * mm, "mid": v(14.78, -5.16) * mm, "end": v(15.96, -5.68) * mm});
            skArc(sketch, "E23.69.1", {"start": v(15.96, -5.68) * mm, "mid": v(16.82, -6.7) * mm, "end": v(17.93, -7.47) * mm});
            skArc(sketch, "E23.69.2", {"start": v(13.55, -4.89) * mm, "mid": v(14.6, -5.66) * mm, "end": v(15.75, -6.23) * mm});
            skArc(sketch, "E23.69.3", {"start": v(15.75, -6.23) * mm, "mid": v(16.58, -7.28) * mm, "end": v(17.72, -8) * mm});
            skLineSegment(sketch, "E23.69.4", {"start": v(13.55, -4.89) * mm, "end": v(13.76, -4.36) * mm});
            skLineSegment(sketch, "E23.69.5", {"start": v(17.93, -7.47) * mm, "end": v(17.72, -8) * mm});
            skArc(sketch, "E23.70.0", {"start": v(14, -3.49) * mm, "mid": v(15.07, -4.23) * mm, "end": v(16.29, -4.67) * mm});
            skArc(sketch, "E23.70.1", {"start": v(16.29, -4.67) * mm, "mid": v(17.21, -5.64) * mm, "end": v(18.36, -6.33) * mm});
            skArc(sketch, "E23.70.2", {"start": v(13.84, -4.03) * mm, "mid": v(14.92, -4.73) * mm, "end": v(16.1, -5.23) * mm});
            skArc(sketch, "E23.70.3", {"start": v(16.1, -5.23) * mm, "mid": v(17, -6.23) * mm, "end": v(18.18, -6.87) * mm});
            skLineSegment(sketch, "E23.70.4", {"start": v(13.84, -4.03) * mm, "end": v(14, -3.49) * mm});
            skLineSegment(sketch, "E23.70.5", {"start": v(18.36, -6.33) * mm, "end": v(18.18, -6.87) * mm});
            skArc(sketch, "E23.71.0", {"start": v(14.2, -2.6) * mm, "mid": v(15.3, -3.27) * mm, "end": v(16.55, -3.64) * mm});
            skArc(sketch, "E23.71.1", {"start": v(16.55, -3.64) * mm, "mid": v(17.53, -4.55) * mm, "end": v(18.72, -5.16) * mm});
            skArc(sketch, "E23.71.2", {"start": v(14.06, -3.15) * mm, "mid": v(15.19, -3.78) * mm, "end": v(16.4, -4.21) * mm});
            skArc(sketch, "E23.71.3", {"start": v(16.4, -4.21) * mm, "mid": v(17.36, -5.15) * mm, "end": v(18.58, -5.71) * mm});
            skLineSegment(sketch, "E23.71.4", {"start": v(14.06, -3.15) * mm, "end": v(14.2, -2.6) * mm});
            skLineSegment(sketch, "E23.71.5", {"start": v(18.72, -5.16) * mm, "end": v(18.58, -5.71) * mm});
            skArc(sketch, "E23.72.0", {"start": v(14.34, -1.7) * mm, "mid": v(15.48, -2.3) * mm, "end": v(16.75, -2.59) * mm});
            skArc(sketch, "E23.72.1", {"start": v(16.75, -2.59) * mm, "mid": v(17.78, -3.44) * mm, "end": v(19, -3.98) * mm});
            skArc(sketch, "E23.72.2", {"start": v(14.23, -2.26) * mm, "mid": v(15.4, -2.82) * mm, "end": v(16.64, -3.17) * mm});
            skArc(sketch, "E23.72.3", {"start": v(16.64, -3.17) * mm, "mid": v(17.65, -4.05) * mm, "end": v(18.9, -4.53) * mm});
            skLineSegment(sketch, "E23.72.4", {"start": v(14.23, -2.26) * mm, "end": v(14.34, -1.7) * mm});
            skLineSegment(sketch, "E23.72.5", {"start": v(19, -3.98) * mm, "end": v(18.9, -4.53) * mm});
            skArc(sketch, "E23.73.0", {"start": v(14.42, -0.8) * mm, "mid": v(15.6, -1.33) * mm, "end": v(16.88, -1.53) * mm});
            skArc(sketch, "E23.73.1", {"start": v(16.88, -1.53) * mm, "mid": v(17.96, -2.31) * mm, "end": v(19.22, -2.78) * mm});
            skArc(sketch, "E23.73.2", {"start": v(14.34, -1.36) * mm, "mid": v(15.54, -1.85) * mm, "end": v(16.8, -2.12) * mm});
            skArc(sketch, "E23.73.3", {"start": v(16.8, -2.12) * mm, "mid": v(17.87, -2.93) * mm, "end": v(19.15, -3.34) * mm});
            skLineSegment(sketch, "E23.73.4", {"start": v(14.34, -1.36) * mm, "end": v(14.42, -0.8) * mm});
            skLineSegment(sketch, "E23.73.5", {"start": v(19.22, -2.78) * mm, "end": v(19.15, -3.34) * mm});
            skArc(sketch, "E23.74.0", {"start": v(14.44, 0.1) * mm, "mid": v(15.65, -0.35) * mm, "end": v(16.94, -0.47) * mm});
            skArc(sketch, "E23.74.1", {"start": v(16.94, -0.47) * mm, "mid": v(18.07, -1.18) * mm, "end": v(19.36, -1.56) * mm});
            skArc(sketch, "E23.74.2", {"start": v(14.4, -0.46) * mm, "mid": v(15.63, -0.87) * mm, "end": v(16.9, -1.06) * mm});
            skArc(sketch, "E23.74.3", {"start": v(16.9, -1.06) * mm, "mid": v(18.02, -1.8) * mm, "end": v(19.32, -2.13) * mm});
            skLineSegment(sketch, "E23.74.4", {"start": v(14.4, -0.46) * mm, "end": v(14.44, 0.1) * mm});
            skLineSegment(sketch, "E23.74.5", {"start": v(19.36, -1.56) * mm, "end": v(19.32, -2.13) * mm});
            skArc(sketch, "E23.75.0", {"start": v(14.4, 1.01) * mm, "mid": v(15.64, 0.64) * mm, "end": v(16.93, 0.6) * mm});
            skArc(sketch, "E23.75.1", {"start": v(16.93, 0.6) * mm, "mid": v(18.11, -0.04) * mm, "end": v(19.42, -0.34) * mm});
            skArc(sketch, "E23.75.2", {"start": v(14.4, 0.45) * mm, "mid": v(15.65, 0.11) * mm, "end": v(16.93, 0) * mm});
            skArc(sketch, "E23.75.3", {"start": v(16.93, 0) * mm, "mid": v(18.1, -0.67) * mm, "end": v(19.42, -0.91) * mm});
            skLineSegment(sketch, "E23.75.4", {"start": v(14.4, 0.45) * mm, "end": v(14.4, 1.01) * mm});
            skLineSegment(sketch, "E23.75.5", {"start": v(19.42, -0.34) * mm, "end": v(19.42, -0.91) * mm});
            skArc(sketch, "E23.76.0", {"start": v(14.31, 1.91) * mm, "mid": v(15.57, 1.62) * mm, "end": v(16.86, 1.66) * mm});
            skArc(sketch, "E23.76.1", {"start": v(16.86, 1.66) * mm, "mid": v(18.08, 1.1) * mm, "end": v(19.4, 0.87) * mm});
            skArc(sketch, "E23.76.2", {"start": v(14.35, 1.35) * mm, "mid": v(15.61, 1.1) * mm, "end": v(16.9, 1.06) * mm});
            skArc(sketch, "E23.76.3", {"start": v(16.9, 1.06) * mm, "mid": v(18.1, 0.47) * mm, "end": v(19.44, 0.31) * mm});
            skLineSegment(sketch, "E23.76.4", {"start": v(14.35, 1.35) * mm, "end": v(14.31, 1.91) * mm});
            skLineSegment(sketch, "E23.76.5", {"start": v(19.4, 0.87) * mm, "end": v(19.44, 0.31) * mm});
            skArc(sketch, "E23.77.0", {"start": v(14.16, 2.8) * mm, "mid": v(15.44, 2.6) * mm, "end": v(16.73, 2.71) * mm});
            skArc(sketch, "E23.77.1", {"start": v(16.73, 2.71) * mm, "mid": v(17.97, 2.23) * mm, "end": v(19.3, 2.1) * mm});
            skArc(sketch, "E23.77.2", {"start": v(14.23, 2.25) * mm, "mid": v(15.51, 2.07) * mm, "end": v(16.8, 2.12) * mm});
            skArc(sketch, "E23.77.3", {"start": v(16.8, 2.12) * mm, "mid": v(18.04, 1.6) * mm, "end": v(19.38, 1.53) * mm});
            skLineSegment(sketch, "E23.77.4", {"start": v(14.23, 2.25) * mm, "end": v(14.16, 2.8) * mm});
            skLineSegment(sketch, "E23.77.5", {"start": v(19.3, 2.1) * mm, "end": v(19.38, 1.53) * mm});
            skArc(sketch, "E23.78.0", {"start": v(13.96, 3.7) * mm, "mid": v(15.24, 3.56) * mm, "end": v(16.52, 3.76) * mm});
            skArc(sketch, "E23.78.1", {"start": v(16.52, 3.76) * mm, "mid": v(17.8, 3.35) * mm, "end": v(19.14, 3.3) * mm});
            skArc(sketch, "E23.78.2", {"start": v(14.06, 3.14) * mm, "mid": v(15.35, 3.04) * mm, "end": v(16.64, 3.17) * mm});
            skArc(sketch, "E23.78.3", {"start": v(16.64, 3.17) * mm, "mid": v(17.9, 2.74) * mm, "end": v(19.24, 2.74) * mm});
            skLineSegment(sketch, "E23.78.4", {"start": v(14.06, 3.14) * mm, "end": v(13.96, 3.7) * mm});
            skLineSegment(sketch, "E23.78.5", {"start": v(19.14, 3.3) * mm, "end": v(19.24, 2.74) * mm});
            skArc(sketch, "E23.79.0", {"start": v(13.7, 4.56) * mm, "mid": v(15, 4.5) * mm, "end": v(16.26, 4.79) * mm});
            skArc(sketch, "E23.79.1", {"start": v(16.26, 4.79) * mm, "mid": v(17.55, 4.46) * mm, "end": v(18.9, 4.5) * mm});
            skArc(sketch, "E23.79.2", {"start": v(13.84, 4.01) * mm, "mid": v(15.13, 4) * mm, "end": v(16.4, 4.21) * mm});
            skArc(sketch, "E23.79.3", {"start": v(16.4, 4.21) * mm, "mid": v(17.7, 3.85) * mm, "end": v(19.03, 3.95) * mm});
            skLineSegment(sketch, "E23.79.4", {"start": v(13.84, 4.01) * mm, "end": v(13.7, 4.56) * mm});
            skLineSegment(sketch, "E23.79.5", {"start": v(18.9, 4.5) * mm, "end": v(19.03, 3.95) * mm});
            skArc(sketch, "E23.80.0", {"start": v(13.38, 5.41) * mm, "mid": v(14.68, 5.44) * mm, "end": v(15.92, 5.8) * mm});
            skArc(sketch, "E23.80.1", {"start": v(15.92, 5.8) * mm, "mid": v(17.24, 5.56) * mm, "end": v(18.57, 5.67) * mm});
            skArc(sketch, "E23.80.2", {"start": v(13.56, 4.87) * mm, "mid": v(14.85, 4.94) * mm, "end": v(16.1, 5.23) * mm});
            skArc(sketch, "E23.80.3", {"start": v(16.1, 5.23) * mm, "mid": v(17.42, 4.96) * mm, "end": v(18.75, 5.13) * mm});
            skLineSegment(sketch, "E23.80.4", {"start": v(13.56, 4.87) * mm, "end": v(13.38, 5.41) * mm});
            skLineSegment(sketch, "E23.80.5", {"start": v(18.57, 5.67) * mm, "end": v(18.75, 5.13) * mm});
            skArc(sketch, "E23.81.0", {"start": v(13.02, 6.24) * mm, "mid": v(14.3, 6.35) * mm, "end": v(15.53, 6.79) * mm});
            skArc(sketch, "E23.81.1", {"start": v(15.53, 6.79) * mm, "mid": v(16.86, 6.63) * mm, "end": v(18.18, 6.83) * mm});
            skArc(sketch, "E23.81.2", {"start": v(13.23, 5.72) * mm, "mid": v(14.5, 5.87) * mm, "end": v(15.75, 6.23) * mm});
            skArc(sketch, "E23.81.3", {"start": v(15.75, 6.23) * mm, "mid": v(17.07, 6.04) * mm, "end": v(18.39, 6.3) * mm});
            skLineSegment(sketch, "E23.81.4", {"start": v(13.23, 5.72) * mm, "end": v(13.02, 6.24) * mm});
            skLineSegment(sketch, "E23.81.5", {"start": v(18.18, 6.83) * mm, "end": v(18.39, 6.3) * mm});
            skArc(sketch, "E23.82.0", {"start": v(12.6, 7.05) * mm, "mid": v(13.88, 7.24) * mm, "end": v(15.07, 7.75) * mm});
            skArc(sketch, "E23.82.1", {"start": v(15.07, 7.75) * mm, "mid": v(16.4, 7.67) * mm, "end": v(17.72, 7.95) * mm});
            skArc(sketch, "E23.82.2", {"start": v(12.84, 6.54) * mm, "mid": v(14.11, 6.76) * mm, "end": v(15.32, 7.21) * mm});
            skArc(sketch, "E23.82.3", {"start": v(15.32, 7.21) * mm, "mid": v(16.66, 7.1) * mm, "end": v(17.96, 7.44) * mm});
            skLineSegment(sketch, "E23.82.4", {"start": v(12.84, 6.54) * mm, "end": v(12.6, 7.05) * mm});
            skLineSegment(sketch, "E23.82.5", {"start": v(17.72, 7.95) * mm, "end": v(17.96, 7.44) * mm});
            skArc(sketch, "E23.83.0", {"start": v(12.13, 7.83) * mm, "mid": v(13.4, 8.1) * mm, "end": v(14.55, 8.68) * mm});
            skArc(sketch, "E23.83.1", {"start": v(14.55, 8.68) * mm, "mid": v(15.9, 8.69) * mm, "end": v(17.18, 9.05) * mm});
            skArc(sketch, "E23.83.2", {"start": v(12.4, 7.33) * mm, "mid": v(13.66, 7.64) * mm, "end": v(14.84, 8.16) * mm});
            skArc(sketch, "E23.83.3", {"start": v(14.84, 8.16) * mm, "mid": v(16.18, 8.13) * mm, "end": v(17.45, 8.56) * mm});
            skLineSegment(sketch, "E23.83.4", {"start": v(12.4, 7.33) * mm, "end": v(12.13, 7.83) * mm});
            skLineSegment(sketch, "E23.83.5", {"start": v(17.18, 9.05) * mm, "end": v(17.45, 8.56) * mm});
            skArc(sketch, "E23.84.0", {"start": v(11.62, 8.57) * mm, "mid": v(12.86, 8.92) * mm, "end": v(13.98, 9.58) * mm});
            skArc(sketch, "E23.84.1", {"start": v(13.98, 9.58) * mm, "mid": v(15.32, 9.67) * mm, "end": v(16.58, 10.11) * mm});
            skArc(sketch, "E23.84.2", {"start": v(11.92, 8.1) * mm, "mid": v(13.15, 8.48) * mm, "end": v(14.3, 9.07) * mm});
            skArc(sketch, "E23.84.3", {"start": v(14.3, 9.07) * mm, "mid": v(15.64, 9.13) * mm, "end": v(16.88, 9.63) * mm});
            skLineSegment(sketch, "E23.84.4", {"start": v(11.92, 8.1) * mm, "end": v(11.62, 8.57) * mm});
            skLineSegment(sketch, "E23.84.5", {"start": v(16.58, 10.11) * mm, "end": v(16.88, 9.63) * mm});
            skArc(sketch, "E23.85.0", {"start": v(11.06, 9.28) * mm, "mid": v(12.28, 9.7) * mm, "end": v(13.35, 10.43) * mm});
            skArc(sketch, "E23.85.1", {"start": v(13.35, 10.43) * mm, "mid": v(14.68, 10.61) * mm, "end": v(15.91, 11.13) * mm});
            skArc(sketch, "E23.85.2", {"start": v(11.39, 8.83) * mm, "mid": v(12.6, 9.29) * mm, "end": v(13.7, 9.95) * mm});
            skArc(sketch, "E23.85.3", {"start": v(13.7, 9.95) * mm, "mid": v(15.03, 10.1) * mm, "end": v(16.24, 10.68) * mm});
            skLineSegment(sketch, "E23.85.4", {"start": v(11.39, 8.83) * mm, "end": v(11.06, 9.28) * mm});
            skLineSegment(sketch, "E23.85.5", {"start": v(15.91, 11.13) * mm, "end": v(16.24, 10.68) * mm});
            skArc(sketch, "E23.86.0", {"start": v(10.45, 9.96) * mm, "mid": v(11.65, 10.46) * mm, "end": v(12.67, 11.25) * mm});
            skArc(sketch, "E23.86.1", {"start": v(12.67, 11.25) * mm, "mid": v(13.98, 11.51) * mm, "end": v(15.18, 12.11) * mm});
            skArc(sketch, "E23.86.2", {"start": v(10.81, 9.52) * mm, "mid": v(11.99, 10.06) * mm, "end": v(13.05, 10.8) * mm});
            skArc(sketch, "E23.86.3", {"start": v(13.05, 10.8) * mm, "mid": v(14.37, 11.02) * mm, "end": v(15.54, 11.67) * mm});
            skLineSegment(sketch, "E23.86.4", {"start": v(10.81, 9.52) * mm, "end": v(10.45, 9.96) * mm});
            skLineSegment(sketch, "E23.86.5", {"start": v(15.18, 12.11) * mm, "end": v(15.54, 11.67) * mm});
            skArc(sketch, "E23.87.0", {"start": v(9.8, 10.6) * mm, "mid": v(10.97, 11.17) * mm, "end": v(11.94, 12.03) * mm});
            skArc(sketch, "E23.87.1", {"start": v(11.94, 12.03) * mm, "mid": v(13.23, 12.37) * mm, "end": v(14.39, 13.04) * mm});
            skArc(sketch, "E23.87.2", {"start": v(10.2, 10.18) * mm, "mid": v(11.33, 10.8) * mm, "end": v(12.35, 11.6) * mm});
            skArc(sketch, "E23.87.3", {"start": v(12.35, 11.6) * mm, "mid": v(13.65, 11.9) * mm, "end": v(14.78, 12.63) * mm});
            skLineSegment(sketch, "E23.87.4", {"start": v(10.2, 10.18) * mm, "end": v(9.8, 10.6) * mm});
            skLineSegment(sketch, "E23.87.5", {"start": v(14.39, 13.04) * mm, "end": v(14.78, 12.63) * mm});
            skArc(sketch, "E23.88.0", {"start": v(9.12, 11.2) * mm, "mid": v(10.24, 11.84) * mm, "end": v(11.16, 12.75) * mm});
            skArc(sketch, "E23.88.1", {"start": v(11.16, 12.75) * mm, "mid": v(12.43, 13.17) * mm, "end": v(13.54, 13.92) * mm});
            skArc(sketch, "E23.88.2", {"start": v(9.53, 10.8) * mm, "mid": v(10.63, 11.48) * mm, "end": v(11.6, 12.35) * mm});
            skArc(sketch, "E23.88.3", {"start": v(11.6, 12.35) * mm, "mid": v(12.88, 12.74) * mm, "end": v(13.96, 13.53) * mm});
            skLineSegment(sketch, "E23.88.4", {"start": v(9.53, 10.8) * mm, "end": v(9.12, 11.2) * mm});
            skLineSegment(sketch, "E23.88.5", {"start": v(13.54, 13.92) * mm, "end": v(13.96, 13.53) * mm});
            skArc(sketch, "E23.89.0", {"start": v(8.4, 11.74) * mm, "mid": v(9.48, 12.46) * mm, "end": v(10.34, 13.43) * mm});
            skArc(sketch, "E23.89.1", {"start": v(10.34, 13.43) * mm, "mid": v(11.58, 13.93) * mm, "end": v(12.64, 14.74) * mm});
            skArc(sketch, "E23.89.2", {"start": v(8.84, 11.38) * mm, "mid": v(9.89, 12.13) * mm, "end": v(10.8, 13.05) * mm});
            skArc(sketch, "E23.89.3", {"start": v(10.8, 13.05) * mm, "mid": v(12.05, 13.52) * mm, "end": v(13.08, 14.38) * mm});
            skLineSegment(sketch, "E23.89.4", {"start": v(8.84, 11.38) * mm, "end": v(8.4, 11.74) * mm});
            skLineSegment(sketch, "E23.89.5", {"start": v(12.64, 14.74) * mm, "end": v(13.08, 14.38) * mm});
            skArc(sketch, "E23.90.0", {"start": v(7.65, 12.25) * mm, "mid": v(8.68, 13.03) * mm, "end": v(9.47, 14.05) * mm});
            skArc(sketch, "E23.90.1", {"start": v(9.47, 14.05) * mm, "mid": v(10.68, 14.63) * mm, "end": v(11.7, 15.5) * mm});
            skArc(sketch, "E23.90.2", {"start": v(8.1, 11.91) * mm, "mid": v(9.1, 12.73) * mm, "end": v(9.95, 13.7) * mm});
            skArc(sketch, "E23.90.3", {"start": v(9.95, 13.7) * mm, "mid": v(11.18, 14.25) * mm, "end": v(12.15, 15.17) * mm});
            skLineSegment(sketch, "E23.90.4", {"start": v(8.1, 11.91) * mm, "end": v(7.65, 12.25) * mm});
            skLineSegment(sketch, "E23.90.5", {"start": v(11.7, 15.5) * mm, "end": v(12.15, 15.17) * mm});
            skArc(sketch, "E23.91.0", {"start": v(6.86, 12.7) * mm, "mid": v(7.84, 13.55) * mm, "end": v(8.57, 14.62) * mm});
            skArc(sketch, "E23.91.1", {"start": v(8.57, 14.62) * mm, "mid": v(9.74, 15.27) * mm, "end": v(10.7, 16.2) * mm});
            skArc(sketch, "E23.91.2", {"start": v(7.34, 12.4) * mm, "mid": v(8.3, 13.27) * mm, "end": v(9.07, 14.3) * mm});
            skArc(sketch, "E23.91.3", {"start": v(9.07, 14.3) * mm, "mid": v(10.26, 14.92) * mm, "end": v(11.17, 15.9) * mm});
            skLineSegment(sketch, "E23.91.4", {"start": v(7.34, 12.4) * mm, "end": v(6.86, 12.7) * mm});
            skLineSegment(sketch, "E23.91.5", {"start": v(10.7, 16.2) * mm, "end": v(11.17, 15.9) * mm});
            skArc(sketch, "E23.92.0", {"start": v(6.05, 13.1) * mm, "mid": v(6.98, 14.01) * mm, "end": v(7.64, 15.13) * mm});
            skArc(sketch, "E23.92.1", {"start": v(7.64, 15.13) * mm, "mid": v(8.76, 15.85) * mm, "end": v(9.66, 16.85) * mm});
            skArc(sketch, "E23.92.2", {"start": v(6.55, 12.84) * mm, "mid": v(7.44, 13.77) * mm, "end": v(8.16, 14.84) * mm});
            skArc(sketch, "E23.92.3", {"start": v(8.16, 14.84) * mm, "mid": v(9.3, 15.54) * mm, "end": v(10.15, 16.58) * mm});
            skLineSegment(sketch, "E23.92.4", {"start": v(6.55, 12.84) * mm, "end": v(6.05, 13.1) * mm});
            skLineSegment(sketch, "E23.92.5", {"start": v(9.66, 16.85) * mm, "end": v(10.15, 16.58) * mm});
            skArc(sketch, "E23.93.0", {"start": v(5.22, 13.46) * mm, "mid": v(6.08, 14.42) * mm, "end": v(6.67, 15.58) * mm});
            skArc(sketch, "E23.93.1", {"start": v(6.67, 15.58) * mm, "mid": v(7.75, 16.37) * mm, "end": v(8.58, 17.42) * mm});
            skArc(sketch, "E23.93.2", {"start": v(5.73, 13.22) * mm, "mid": v(6.56, 14.2) * mm, "end": v(7.21, 15.32) * mm});
            skArc(sketch, "E23.93.3", {"start": v(7.21, 15.32) * mm, "mid": v(8.3, 16.1) * mm, "end": v(9.1, 17.18) * mm});
            skLineSegment(sketch, "E23.93.4", {"start": v(5.73, 13.22) * mm, "end": v(5.22, 13.46) * mm});
            skLineSegment(sketch, "E23.93.5", {"start": v(8.58, 17.42) * mm, "end": v(9.1, 17.18) * mm});
            skArc(sketch, "E23.94.0", {"start": v(4.36, 13.76) * mm, "mid": v(5.16, 14.78) * mm, "end": v(5.68, 15.96) * mm});
            skArc(sketch, "E23.94.1", {"start": v(5.68, 15.96) * mm, "mid": v(6.7, 16.82) * mm, "end": v(7.47, 17.93) * mm});
            skArc(sketch, "E23.94.2", {"start": v(4.89, 13.55) * mm, "mid": v(5.66, 14.6) * mm, "end": v(6.23, 15.75) * mm});
            skArc(sketch, "E23.94.3", {"start": v(6.23, 15.75) * mm, "mid": v(7.28, 16.58) * mm, "end": v(8, 17.72) * mm});
            skLineSegment(sketch, "E23.94.4", {"start": v(4.89, 13.55) * mm, "end": v(4.36, 13.76) * mm});
            skLineSegment(sketch, "E23.94.5", {"start": v(7.47, 17.93) * mm, "end": v(8, 17.72) * mm});
            skArc(sketch, "E23.95.0", {"start": v(3.49, 14) * mm, "mid": v(4.23, 15.07) * mm, "end": v(4.67, 16.29) * mm});
            skArc(sketch, "E23.95.1", {"start": v(4.67, 16.29) * mm, "mid": v(5.64, 17.21) * mm, "end": v(6.33, 18.36) * mm});
            skArc(sketch, "E23.95.2", {"start": v(4.03, 13.84) * mm, "mid": v(4.73, 14.92) * mm, "end": v(5.23, 16.1) * mm});
            skArc(sketch, "E23.95.3", {"start": v(5.23, 16.1) * mm, "mid": v(6.23, 17) * mm, "end": v(6.87, 18.18) * mm});
            skLineSegment(sketch, "E23.95.4", {"start": v(4.03, 13.84) * mm, "end": v(3.49, 14) * mm});
            skLineSegment(sketch, "E23.95.5", {"start": v(6.33, 18.36) * mm, "end": v(6.87, 18.18) * mm});
            skArc(sketch, "E23.96.0", {"start": v(2.6, 14.2) * mm, "mid": v(3.27, 15.3) * mm, "end": v(3.64, 16.55) * mm});
            skArc(sketch, "E23.96.1", {"start": v(3.64, 16.55) * mm, "mid": v(4.55, 17.53) * mm, "end": v(5.16, 18.72) * mm});
            skArc(sketch, "E23.96.2", {"start": v(3.15, 14.06) * mm, "mid": v(3.78, 15.19) * mm, "end": v(4.21, 16.4) * mm});
            skArc(sketch, "E23.96.3", {"start": v(4.21, 16.4) * mm, "mid": v(5.15, 17.36) * mm, "end": v(5.71, 18.58) * mm});
            skLineSegment(sketch, "E23.96.4", {"start": v(3.15, 14.06) * mm, "end": v(2.6, 14.2) * mm});
            skLineSegment(sketch, "E23.96.5", {"start": v(5.16, 18.72) * mm, "end": v(5.71, 18.58) * mm});
            skArc(sketch, "E23.97.0", {"start": v(1.7, 14.34) * mm, "mid": v(2.3, 15.48) * mm, "end": v(2.59, 16.75) * mm});
            skArc(sketch, "E23.97.1", {"start": v(2.59, 16.75) * mm, "mid": v(3.44, 17.78) * mm, "end": v(3.98, 19) * mm});
            skArc(sketch, "E23.97.2", {"start": v(2.26, 14.23) * mm, "mid": v(2.82, 15.4) * mm, "end": v(3.17, 16.64) * mm});
            skArc(sketch, "E23.97.3", {"start": v(3.17, 16.64) * mm, "mid": v(4.05, 17.65) * mm, "end": v(4.53, 18.9) * mm});
            skLineSegment(sketch, "E23.97.4", {"start": v(2.26, 14.23) * mm, "end": v(1.7, 14.34) * mm});
            skLineSegment(sketch, "E23.97.5", {"start": v(3.98, 19) * mm, "end": v(4.53, 18.9) * mm});
            skArc(sketch, "E23.98.0", {"start": v(0.8, 14.42) * mm, "mid": v(1.33, 15.6) * mm, "end": v(1.53, 16.88) * mm});
            skArc(sketch, "E23.98.1", {"start": v(1.53, 16.88) * mm, "mid": v(2.31, 17.96) * mm, "end": v(2.78, 19.22) * mm});
            skArc(sketch, "E23.98.2", {"start": v(1.36, 14.34) * mm, "mid": v(1.85, 15.54) * mm, "end": v(2.12, 16.8) * mm});
            skArc(sketch, "E23.98.3", {"start": v(2.12, 16.8) * mm, "mid": v(2.93, 17.87) * mm, "end": v(3.34, 19.15) * mm});
            skLineSegment(sketch, "E23.98.4", {"start": v(1.36, 14.34) * mm, "end": v(0.8, 14.42) * mm});
            skLineSegment(sketch, "E23.98.5", {"start": v(2.78, 19.22) * mm, "end": v(3.34, 19.15) * mm});
            skArc(sketch, "E23.99.0", {"start": v(-0.1, 14.44) * mm, "mid": v(0.35, 15.65) * mm, "end": v(0.47, 16.94) * mm});
            skArc(sketch, "E23.99.1", {"start": v(0.47, 16.94) * mm, "mid": v(1.18, 18.07) * mm, "end": v(1.56, 19.36) * mm});
            skArc(sketch, "E23.99.2", {"start": v(0.46, 14.4) * mm, "mid": v(0.87, 15.63) * mm, "end": v(1.06, 16.9) * mm});
            skArc(sketch, "E23.99.3", {"start": v(1.06, 16.9) * mm, "mid": v(1.8, 18.02) * mm, "end": v(2.13, 19.32) * mm});
            skLineSegment(sketch, "E23.99.4", {"start": v(0.46, 14.4) * mm, "end": v(-0.1, 14.44) * mm});
            skLineSegment(sketch, "E23.99.5", {"start": v(1.56, 19.36) * mm, "end": v(2.13, 19.32) * mm});
            skPoint(sketch, "E23.center", {"position": v(0, 0) * mm});
            skSolve(sketch);
        }
        {
            var Q0;
            Q0 = qSketchRegion(id + "F8", true);
            extrude(context, id + "F9", {"entities" : qUnion([Q0]), "operationType" : NewBodyOperationType.ADD, "depth" : 10 * mm});
        }
    });
